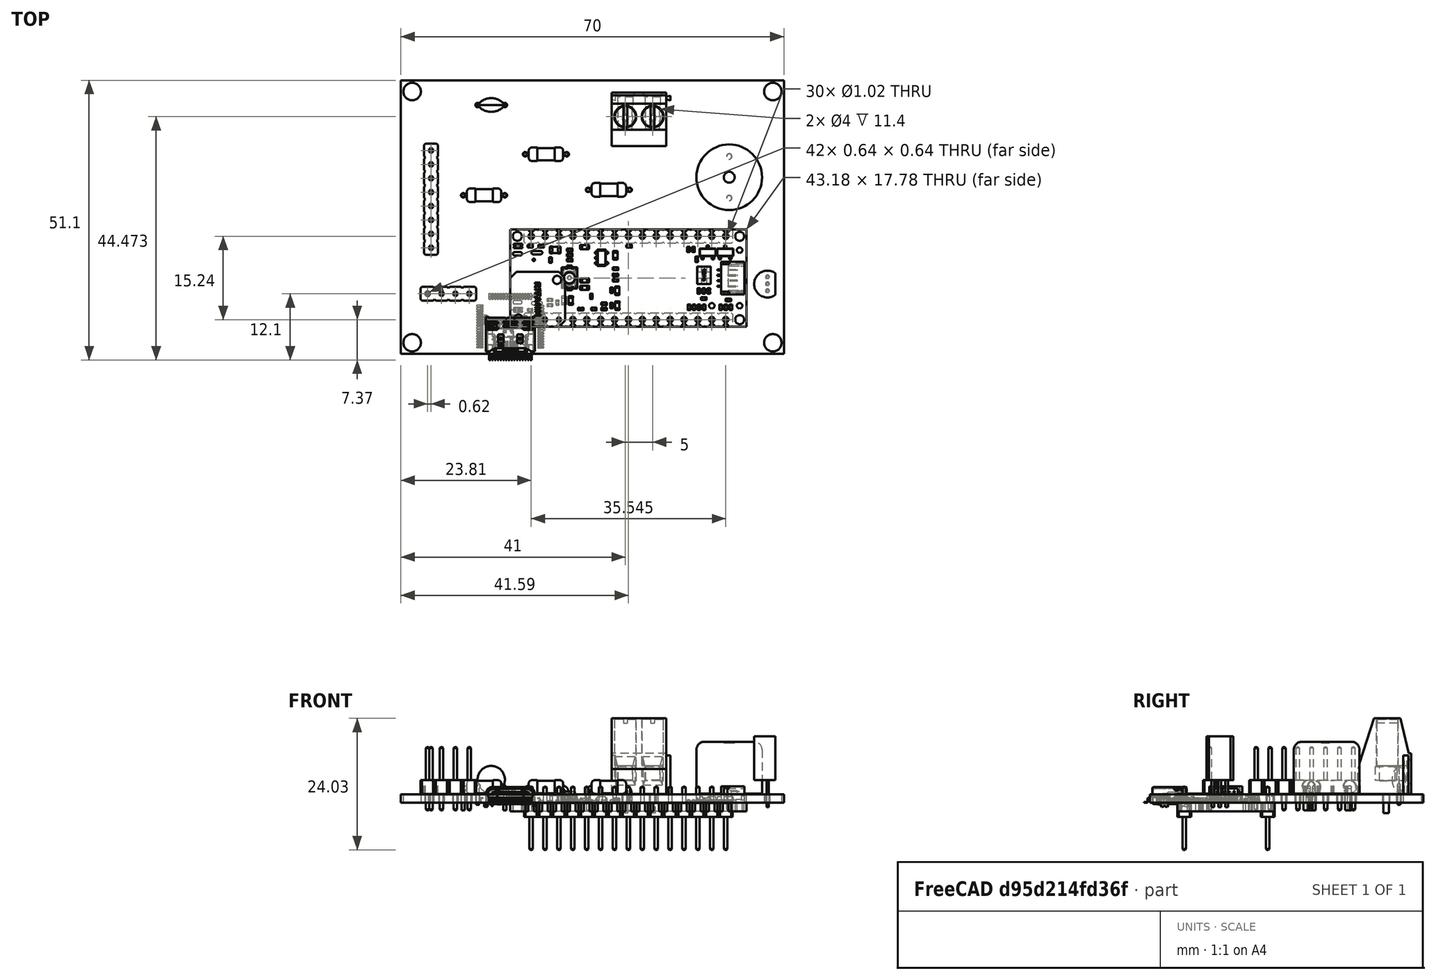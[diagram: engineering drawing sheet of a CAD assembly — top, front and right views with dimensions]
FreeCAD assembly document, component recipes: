
FREECAD ASSEMBLY — COMPONENT RECIPES ("assembly_Pendulum_fusion")

This assembly document has 14 components, labeled P0..P13 below (a component is one placed body or linked part). 12 of them carry a construction recipe — the FreeCAD feature program that regenerates the part from scratch, quoted from this document or its linked companion documents; the rest are supplied as boundary geometry only. No exploded tour is included for this assembly.
COMPONENT P0 — recipe-attached ("Body_Battery_Tattu", modeled in this document).
Construction recipe (the document's own serialized feature program — sketch geometry with constraints, then the solid features built on it; lengths are millimeters unless a unit is written):

FEATURE [Sketcher::SketchObject] Sketch048
  ArcFitTolerance = 1e-06
  AttachmentSupport = -> [XZ_Plane110]
  FullyConstrained = true
  MakeInternals = false
  MapMode = 5
  Placement = pos=(0,0,0) rot=(1,0,0;1.5708rad)
  sketch-geometry (6):
    g0: Circle CenterX=8.5 CenterY=-6.5 CenterZ=0 NormalX=0 NormalY=0 NormalZ=1 AngleXU=0 Radius=1.5
    g1: Circle CenterX=-8.5 CenterY=-6.5 CenterZ=0 NormalX=0 NormalY=0 NormalZ=1 AngleXU=0 Radius=1.5
    g2: Circle CenterX=-5.3 CenterY=-6.5 CenterZ=0 NormalX=0 NormalY=0 NormalZ=1 AngleXU=0 Radius=0.8
    g3: Circle CenterX=-2.8 CenterY=-6.5 CenterZ=0 NormalX=0 NormalY=0 NormalZ=1 AngleXU=0 Radius=0.8
    g4: Circle CenterX=2.8 CenterY=-6.5 CenterZ=0 NormalX=0 NormalY=0 NormalZ=1 AngleXU=0 Radius=0.8
    g5: Circle CenterX=5.3 CenterY=-6.5 CenterZ=0 NormalX=0 NormalY=0 NormalZ=1 AngleXU=0 Radius=0.8
  constraints (15):
    c: Equal(g0,g1)
    c: Equal(g5,g4)
    c: Equal(g4,g3)
    c: Equal(g3,g2)
    c: Symmetric(g0,g1,g-2)
    c: Diameter(g0) = 3
    c: DistanceX(g1,g0) = 17
    c: DistanceY(g0,g-1) = 6.5
    c: Diameter(g2) = 1.6
    c: Symmetric(g5,g2,g-2)
    c: Symmetric(g4,g3,g-2)
    c: DistanceX(g3,g4) = 5.6
    c: DistanceX(g2,g5) = 10.6
    c: DistanceY(g5,g-1) = 6.5
    c: DistanceY(g4,g-1) = 6.5
FEATURE [Sketcher::SketchObject] Sketch049
  ArcFitTolerance = 1e-06
  AttachmentSupport = -> [XZ_Plane110]
  FullyConstrained = true
  MakeInternals = false
  MapMode = 5
  Placement = pos=(0,0,0) rot=(1,0,0;1.5708rad)
  sketch-geometry (4):
    g0: LineSegment StartX=-10 StartY=8 StartZ=0 EndX=-10 EndY=-8 EndZ=0
    g1: LineSegment StartX=-10 StartY=-8 StartZ=0 EndX=10 EndY=-8 EndZ=0
    g2: LineSegment StartX=10 StartY=-8 StartZ=0 EndX=10 EndY=8 EndZ=0
    g3: LineSegment StartX=10 StartY=8 StartZ=0 EndX=-10 EndY=8 EndZ=0
  constraints (11):
    c: Coincident(g0,g1)
    c: Coincident(g1,g2)
    c: Coincident(g2,g3)
    c: Coincident(g3,g0)
    c: Vertical(g0)
    c: Vertical(g2)
    c: Horizontal(g1)
    c: Horizontal(g3)
    c: Symmetric(g1,g0,g-1)
    c: DistanceY(g0,g0) = 16
    c: DistanceX(g1,g1) = 20
FEATURE [PartDesign::Pad] Pad030
  Direction = (0,-1,2e-16)
  Length = 64.5
  Length2 = 10
  Placement = pos=(0,0,0) rot=(1,0,0;1.5708rad)
  Profile = -> Sketch049
  ReferenceAxis = -> Sketch049 [N_Axis]
  Refine = true
  Suppressed = false
  Type = 0
FEATURE [PartDesign::Fillet] Fillet007
  Base = -> Pad030 [Edge10,Edge4]
  BaseFeature = -> Pad030
  Placement = pos=(0,0,0) rot=(1,0,0;1.5708rad)
  Radius = 3
  Refine = true
  SupportTransform = false
  Suppressed = false
  UseAllEdges = false
FEATURE [PartDesign::Fillet] Fillet008
  Base = -> Fillet007 [Edge3,Edge13]
  BaseFeature = -> Fillet007
  Placement = pos=(0,0,0) rot=(1,0,0;1.5708rad)
  Radius = 9
  Refine = true
  SupportTransform = false
  Suppressed = false
  UseAllEdges = false
FEATURE [PartDesign::Pad] Pad031  label="Pad_Battery"
  BaseFeature = -> Fillet008
  Direction = (0,-1,2e-16)
  Length = 10
  Length2 = 10
  Midplane = true
  Placement = pos=(0,0,0) rot=(1,0,0;1.5708rad)
  Profile = -> Sketch048
  ReferenceAxis = -> Sketch048 [N_Axis]
  Refine = true
  Suppressed = false
  Type = 0
FEATURE [PartDesign::CoordinateSystem] Battery
  AttacherType = Attacher::AttachEngine3D
  AttachmentSupport = -> [Pad031]
  MapMode = 45
  Placement = pos=(-7,-64.5,2.89e-14) rot=(0,0,1;0rad)
FEATURE [PartDesign::Body] Body014  label="Body_Battery_Tattu"
  AllowCompound = false
  Group = -> [Sketch049,Pad030,Fillet007,Fillet008,Sketch048,Pad031,Battery]
  Origin = -> Origin110
  Tip = -> Pad031
COMPONENT P1 — recipe-attached ("Body_circuit_house", modeled in this document).
Construction recipe (the document's own serialized feature program — sketch geometry with constraints, then the solid features built on it; lengths are millimeters unless a unit is written):

FEATURE [Sketcher::SketchObject] Sketch064
  ArcFitTolerance = 1e-06
  AttachmentSupport = -> [XY_Plane115]
  FullyConstrained = false
  MakeInternals = false
  MapMode = 5
  sketch-geometry (4):
    g0: LineSegment StartX=-25.456 StartY=35.625 StartZ=0 EndX=-25.456 EndY=-34.975 EndZ=0
    g1: LineSegment StartX=-25.456 StartY=-34.975 StartZ=0 EndX=25.144 EndY=-34.975 EndZ=0
    g2: LineSegment StartX=25.144 StartY=-34.975 StartZ=0 EndX=25.144 EndY=35.625 EndZ=0
    g3: LineSegment StartX=25.144 StartY=35.625 StartZ=0 EndX=-25.456 EndY=35.625 EndZ=0
  constraints (10):
    c: Coincident(g0,g1)
    c: Coincident(g1,g2)
    c: Coincident(g2,g3)
    c: Coincident(g3,g0)
    c: Vertical(g0)
    c: Vertical(g2)
    c: Horizontal(g1)
    c: Horizontal(g3)
    c: DistanceX(g3,g3) = 50.6
    c: DistanceY(g0,g0) = 70.6
FEATURE [Sketcher::SketchObject] Sketch065
  ArcFitTolerance = 1e-06
  AttachmentSupport = -> [XY_Plane115]
  FullyConstrained = true
  MakeInternals = false
  MapMode = 5
  sketch-geometry (12):
    g0: LineSegment StartX=-22.96 StartY=27.96 StartZ=0 EndX=-22.96 EndY=-27.96 EndZ=0
    g1: LineSegment StartX=-17.96 StartY=-32.96 StartZ=0 EndX=17.96 EndY=-32.96 EndZ=0
    g2: LineSegment StartX=22.96 StartY=-27.96 StartZ=0 EndX=22.96 EndY=27.96 EndZ=0
    g3: LineSegment StartX=18.053 StartY=32 StartZ=0 EndX=-18.053 EndY=32 EndZ=0
    g4: LineSegment StartX=-27 StartY=37 StartZ=0 EndX=-27 EndY=-37 EndZ=0
    g5: LineSegment StartX=-27 StartY=-37 StartZ=0 EndX=27 EndY=-37 EndZ=0
    g6: LineSegment StartX=27 StartY=-37 StartZ=0 EndX=27 EndY=37 EndZ=0
    g7: LineSegment StartX=27 StartY=37 StartZ=0 EndX=-27 EndY=37 EndZ=0
    g8: ArcOfCircle CenterX=-22.96 CenterY=32.96 CenterZ=0 NormalX=0 NormalY=0 NormalZ=1 AngleXU=0 Radius=5 StartAngle=4.71239 EndAngle=6.08999
    g9: ArcOfCircle CenterX=22.96 CenterY=32.96 CenterZ=0 NormalX=0 NormalY=0 NormalZ=1 AngleXU=0 Radius=5 StartAngle=3.33479 EndAngle=4.71239
    g10: ArcOfCircle CenterX=22.96 CenterY=-32.96 CenterZ=0 NormalX=0 NormalY=0 NormalZ=1 AngleXU=0 Radius=5 StartAngle=1.5708 EndAngle=3.14159
    g11: ArcOfCircle CenterX=-22.96 CenterY=-32.96 CenterZ=0 NormalX=0 NormalY=0 NormalZ=1 AngleXU=0 Radius=5 StartAngle=3e-16 EndAngle=1.5708
  constraints (34):
    c: Coincident(g4,g5)
    c: Coincident(g5,g6)
    c: Coincident(g6,g7)
    c: Coincident(g7,g4)
    c: Vertical(g4)
    c: Vertical(g6)
    c: Horizontal(g5)
    c: Horizontal(g7)
    c: DistanceX(g7,g7) = 54
    c: DistanceY(g6,g6) = 74
    c: Symmetric(g4,g5,g-1)
    c: Equal(g8,g9)
    c: Equal(g9,g10)
    c: Equal(g10,g11)
    c: Diameter(g9) = 10
    c: Coincident(g3,g8)
    c: Coincident(g0,g8)
    c: Coincident(g3,g9)
    c: Coincident(g2,g9)
    c: Coincident(g0,g11)
    c: Coincident(g1,g11)
    c: Coincident(g1,g10)
    c: Coincident(g2,g10)
    c: Symmetric(g3,g3,g-2)
    c: Symmetric(g0,g0,g-1)
    c: Symmetric(g1,g1,g-2)
    c: Symmetric(g2,g2,g-1)
    c: Symmetric(g8,g10,g-1)
    c: DistanceY(g3,g4) = 5
    c: DistanceY(g10,g8) = 65.92
    c: DistanceX(g11,g10) = 45.92
    c: PointOnObject(g11,g1)
    c: PointOnObject(g8,g0)
    c: PointOnObject(g10,g2)
FEATURE [PartDesign::Pad] Pad040
  Direction = (0,0,1)
  Length = 26
  Length2 = 10
  Profile = -> Sketch065
  ReferenceAxis = -> Sketch065 [N_Axis]
  Refine = true
  Reversed = true
  Suppressed = false
  Type = 0
FEATURE [PartDesign::Pocket] Pocket019
  BaseFeature = -> Pad040
  Direction = (0,0,-1)
  Length = 2
  Length2 = 5
  Profile = -> Sketch064
  ReferenceAxis = -> Sketch064 [N_Axis]
  Refine = true
  Suppressed = false
  Type = 0
FEATURE [Sketcher::SketchObject] Sketch066
  ArcFitTolerance = 1e-06
  AttachmentSupport = -> [Pocket019]
  FullyConstrained = true
  MakeInternals = false
  MapMode = 5
  Placement = pos=(0,0,-2) rot=(0,0,1;0rad)
  sketch-geometry (4):
    g0: Circle CenterX=-22.96 CenterY=32.96 CenterZ=0 NormalX=0 NormalY=0 NormalZ=1 AngleXU=0 Radius=1.3
    g1: Circle CenterX=22.96 CenterY=32.96 CenterZ=0 NormalX=0 NormalY=0 NormalZ=1 AngleXU=0 Radius=1.3
    g2: Circle CenterX=22.96 CenterY=-32.96 CenterZ=0 NormalX=0 NormalY=0 NormalZ=1 AngleXU=0 Radius=1.3
    g3: Circle CenterX=-22.96 CenterY=-32.96 CenterZ=0 NormalX=0 NormalY=0 NormalZ=1 AngleXU=0 Radius=1.3
  constraints (9):
    c: Equal(g0,g1)
    c: Equal(g1,g2)
    c: Equal(g2,g3)
    c: Symmetric(g3,g0,g-1)
    c: Symmetric(g0,g1,g-2)
    c: Symmetric(g3,g2,g-2)
    c: DistanceX(g0,g1) = 45.92
    c: DistanceY(g2,g1) = 65.92
    c: Diameter(g0) = 2.6
FEATURE [PartDesign::Pocket] Pocket020
  BaseFeature = -> Pocket019
  Direction = (0,0,-1)
  Length = 5
  Length2 = 5
  Profile = -> Sketch066
  ReferenceAxis = -> Sketch066 [N_Axis]
  Refine = true
  Suppressed = false
  Type = 1
FEATURE [Sketcher::SketchObject] Sketch067
  ArcFitTolerance = 1e-06
  AttachmentSupport = -> [Pocket020]
  ExternalGeometry = -> [Pocket020]
  FullyConstrained = true
  MakeInternals = false
  MapMode = 5
  Placement = pos=(0,0,-26) rot=(1,0,0;3.14159rad)
  sketch-geometry (6):
    g0: ArcOfCircle CenterX=-27.5 CenterY=42 CenterZ=0 NormalX=0 NormalY=0 NormalZ=1 AngleXU=0 Radius=7 StartAngle=0 EndAngle=4.71239
    g1: ArcOfCircle CenterX=27.5 CenterY=42 CenterZ=0 NormalX=0 NormalY=0 NormalZ=1 AngleXU=0 Radius=7 StartAngle=4.71239 EndAngle=9.42478
    g2: LineSegment StartX=-20.5 StartY=42 StartZ=0 EndX=20.5 EndY=42 EndZ=0
    g3: LineSegment StartX=-27.5 StartY=35 StartZ=0 EndX=27.5 EndY=35 EndZ=0
    g4: Circle CenterX=-27.5 CenterY=42 CenterZ=0 NormalX=0 NormalY=0 NormalZ=1 AngleXU=0 Radius=2.3
    g5: Circle CenterX=27.5 CenterY=42 CenterZ=0 NormalX=0 NormalY=0 NormalZ=1 AngleXU=0 Radius=2.3
  constraints (16):
    c: Horizontal(g2)
    c: Symmetric(g0,g1,g-2)
    c: DistanceX(g0,g1) = 55
    c: Equal(g1,g0)
    c: Diameter(g1) = 14
    c: DistanceY(g-3,g0) = 5
    c: Horizontal(g3)
    c: PointOnObject(g0,g2)
    c: Coincident(g0,g3)
    c: Coincident(g0,g2)
    c: Coincident(g1,g2)
    c: Tangent(g1,g3) = -1.5708
    c: Coincident(g4,g0)
    c: Coincident(g5,g1)
    c: Equal(g5,g4)
    c: Diameter(g5) = 4.6
FEATURE [PartDesign::Pad] Pad041
  BaseFeature = -> Pocket020
  Direction = (0,0,-1)
  Length = 5
  Length2 = 10
  Profile = -> Sketch067
  ReferenceAxis = -> Sketch067 [N_Axis]
  Refine = true
  Reversed = true
  Suppressed = false
  Type = 0
FEATURE [PartDesign::CoordinateSystem] Circuit_House
  AttacherType = Attacher::AttachEngine3D
  AttachmentSupport = -> [Pad041]
  MapMode = 45
  Placement = pos=(27.5,-42,-21) rot=(0,0,0.999999;1.4e-05rad)
FEATURE [PartDesign::CoordinateSystem] Circuit_House_Top
  AttacherType = Attacher::AttachEngine3D
  AttachmentSupport = -> [Pad041]
  MapMode = 45
  Placement = pos=(-22.96,32.96,-2) rot=(0,0,1;0rad)
FEATURE [PartDesign::Body] Body018  label="Body_circuit_house"
  AllowCompound = false
  Group = -> [Sketch065,Pad040,Sketch064,Pocket019,Sketch066,Pocket020,Sketch067,Pad041,Circuit_House,Circuit_House_Top]
  Origin = -> Origin115
  Tip = -> Pad041
COMPONENT P2 — recipe-attached ("Body_Arm001", modeled in this document).
Construction recipe (the document's own serialized feature program — sketch geometry with constraints, then the solid features built on it; lengths are millimeters unless a unit is written):

FEATURE [Sketcher::SketchObject] Sketch006
  ArcFitTolerance = 1e-06
  AttachmentSupport = -> [XY_Plane004]
  FullyConstrained = true
  MakeInternals = false
  MapMode = 5
  sketch-geometry (1):
    g0: Circle CenterX=0 CenterY=84.85 CenterZ=0 NormalX=0 NormalY=0 NormalZ=1 AngleXU=0 Radius=23
  constraints (3):
    c: PointOnObject(g0,g-2)
    c: DistanceY(g-1,g0) = 84.85
    c: Diameter(g0) = 46
FEATURE [Sketcher::SketchObject] Sketch007
  ArcFitTolerance = 1e-06
  AttachmentSupport = -> [XY_Plane004]
  FullyConstrained = true
  MakeInternals = false
  MapMode = 5
  sketch-geometry (33):
    g0: LineSegment StartX=-18 StartY=67.5 StartZ=0 EndX=-18 EndY=-67.5 EndZ=0
    g1: LineSegment StartX=18 StartY=-67.5 StartZ=0 EndX=18 EndY=67.5 EndZ=0
    g2: ArcOfCircle CenterX=0 CenterY=84.8494 CenterZ=0 NormalX=0 NormalY=0 NormalZ=1 AngleXU=0 Radius=25 StartAngle=5.51619 EndAngle=10.1918
    g3: Circle CenterX=0 CenterY=84.8494 CenterZ=0 NormalX=0 NormalY=0 NormalZ=1 AngleXU=0 Radius=11.5
    g4: Circle CenterX=0 CenterY=99.8494 CenterZ=0 NormalX=0 NormalY=0 NormalZ=1 AngleXU=0 Radius=1.8
    g5: Circle CenterX=9.64181 CenterY=96.34 CenterZ=0 NormalX=0 NormalY=0 NormalZ=1 AngleXU=0 Radius=1.8
    g6: Circle CenterX=14.7721 CenterY=87.4541 CenterZ=0 NormalX=0 NormalY=0 NormalZ=1 AngleXU=0 Radius=1.8
    g7: Circle CenterX=12.9904 CenterY=77.3494 CenterZ=0 NormalX=0 NormalY=0 NormalZ=1 AngleXU=0 Radius=1.8
    g8: Circle CenterX=5.1303 CenterY=70.754 CenterZ=0 NormalX=0 NormalY=0 NormalZ=1 AngleXU=0 Radius=1.8
    g9: Circle CenterX=-5.1303 CenterY=70.754 CenterZ=0 NormalX=0 NormalY=0 NormalZ=1 AngleXU=0 Radius=1.8
    g10: Circle CenterX=-12.9904 CenterY=77.3494 CenterZ=0 NormalX=0 NormalY=0 NormalZ=1 AngleXU=0 Radius=1.8
    g11: Circle CenterX=-14.7721 CenterY=87.4541 CenterZ=0 NormalX=0 NormalY=0 NormalZ=1 AngleXU=0 Radius=1.8
    g12: Circle CenterX=-9.64181 CenterY=96.34 CenterZ=0 NormalX=0 NormalY=0 NormalZ=1 AngleXU=0 Radius=1.8
    g13: LineSegment [constr] StartX=-9.64181 StartY=96.34 StartZ=0 EndX=0 EndY=84.8494 EndZ=0
    g14: LineSegment [constr] StartX=-14.7721 StartY=87.4541 StartZ=0 EndX=0 EndY=84.8494 EndZ=0
    g15: LineSegment [constr] StartX=-12.9904 StartY=77.3494 StartZ=0 EndX=0 EndY=84.8494 EndZ=0
    g16: LineSegment [constr] StartX=-5.1303 StartY=70.754 StartZ=0 EndX=0 EndY=84.8494 EndZ=0
    g17: LineSegment [constr] StartX=5.1303 StartY=70.754 StartZ=0 EndX=0 EndY=84.8494 EndZ=0
    g18: LineSegment [constr] StartX=12.9904 StartY=77.3494 StartZ=0 EndX=0 EndY=84.8494 EndZ=0
    g19: LineSegment [constr] StartX=14.7721 StartY=87.4541 StartZ=0 EndX=0 EndY=84.8494 EndZ=0
    g20: LineSegment [constr] StartX=9.64181 StartY=96.34 StartZ=0 EndX=0 EndY=84.8494 EndZ=0
    g21: Circle CenterX=-7.78 CenterY=-27 CenterZ=0 NormalX=0 NormalY=0 NormalZ=1 AngleXU=0 Radius=1.8
    g22: Circle CenterX=7.78 CenterY=-27 CenterZ=0 NormalX=0 NormalY=0 NormalZ=1 AngleXU=0 Radius=1.8
    g23: ArcOfCircle CenterX=0 CenterY=-84.8494 CenterZ=0 NormalX=0 NormalY=0 NormalZ=1 AngleXU=0 Radius=25 StartAngle=2.3746 EndAngle=7.05018
    g24: Circle CenterX=0 CenterY=-84.8494 CenterZ=0 NormalX=0 NormalY=0 NormalZ=1 AngleXU=0 Radius=11.25
    g25: LineSegment StartX=-12.5 StartY=63.1987 StartZ=0 EndX=-12.5 EndY=-16.8013 EndZ=0
    g26: LineSegment StartX=-12.5 StartY=-16.8013 StartZ=0 EndX=12.5 EndY=-16.8013 EndZ=0
    g27: LineSegment StartX=12.5 StartY=-16.8013 StartZ=0 EndX=12.5 EndY=63.1987 EndZ=0
    g28: LineSegment StartX=-12.5 StartY=-33.5 StartZ=0 EndX=-12.5 EndY=-67.5 EndZ=0
    g29: LineSegment StartX=-12.5 StartY=-67.5 StartZ=0 EndX=12.5 EndY=-67.5 EndZ=0
    g30: LineSegment StartX=12.5 StartY=-67.5 StartZ=0 EndX=12.5 EndY=-33.5 EndZ=0
    g31: LineSegment StartX=12.5 StartY=-33.5 StartZ=0 EndX=-12.5 EndY=-33.5 EndZ=0
    g32: ArcOfCircle CenterX=0 CenterY=84.8494 CenterZ=0 NormalX=0 NormalY=0 NormalZ=1 AngleXU=0 Radius=25 StartAngle=4.18879 EndAngle=5.23599
  constraints (88):
    c: Vertical(g0)
    c: Vertical(g1)
    c: Symmetric(g0,g1,g-1)
    c: DistanceX(g0,g1) = 36
    c: DistanceY(g1,g1) = 135
    c: PointOnObject(g2,g-2)
    c: Diameter(g2) = 50
    c: Coincident(g2,g0)
    c: Coincident(g2,g1)
    c: Coincident(g3,g2)
    c: Diameter(g3) = 23
    c: PointOnObject(g4,g-2)
    c: Coincident(g13,g12)
    c: Coincident(g13,g2)
    c: Coincident(g14,g11)
    c: Coincident(g14,g2)
    c: Coincident(g15,g10)
    c: Coincident(g15,g2)
    c: Coincident(g16,g9)
    c: Coincident(g16,g2)
    c: Coincident(g17,g8)
    c: Coincident(g17,g2)
    c: Coincident(g18,g7)
    c: Coincident(g18,g2)
    c: Coincident(g19,g6)
    c: Coincident(g19,g2)
    c: Coincident(g20,g5)
    c: Coincident(g20,g2)
    c: Equal(g4,g5)
    c: Equal(g5,g6)
    c: Equal(g6,g7)
    c: Equal(g7,g8)
    c: Equal(g8,g9)
    c: Equal(g9,g10)
    c: Equal(g10,g11)
    c: Equal(g11,g12)
    c: Equal(g13,g14)
    c: Equal(g14,g15)
    c: Equal(g15,g16)
    c: Equal(g16,g17)
    c: Equal(g17,g18)
    c: Equal(g18,g19)
    c: Equal(g19,g20)
    c: DistanceY(g2,g4) = 15
    c: Distance(g13) = 15
    c: Diameter(g4) = 3.6
    c: Angle(g-2,g20) = 2.44346
    c: Angle(g19,g20) = 0.698132
    c: Angle(g18,g19) = 0.698132
    c: Angle(g17,g18) = 0.698132
    c: Angle(g16,g17) = 0.698132
    c: Angle(g15,g16) = 0.698132
    c: Angle(g14,g15) = 0.698132
    c: Angle(g13,g14) = 0.698132
    c: Equal(g22,g21)
    c: Diameter(g21) = 3.6
    c: DistanceX(g21,g22) = 15.56
    c: Symmetric(g21,g22,g-2)
    c: DistanceY(g22,g-1) = 27
    c: PointOnObject(g23,g-2)
    c: Diameter(g23) = 50
    c: Coincident(g23,g1)
    c: Coincident(g23,g0)
    c: Coincident(g24,g23)
    c: Diameter(g24) = 22.5
    c: Vertical(g25)
    c: Vertical(g27)
    c: Horizontal(g26)
    c: Coincident(g28,g29)
    c: Coincident(g29,g30)
    c: Coincident(g30,g31)
    c: Coincident(g31,g28)
    c: Vertical(g28)
    c: Vertical(g30)
    c: Horizontal(g29)
    c: Symmetric(g27,g25,g-2)
    c: DistanceY(g25,g25) = 80
    c: DistanceX(g25,g27) = 25
    c: PointOnObject(g1,g29)
    c: Symmetric(g28,g30,g-2)
    c: DistanceX(g31,g31) = 25
    c: DistanceY(g28,g28) = 34
    c: Diameter(g32) = 50
    c: Coincident(g32,g25)
    c: Coincident(g32,g27)
    c: Coincident(g32,g2)
    c: Coincident(g26,g25)
    c: Coincident(g27,g26)
FEATURE [PartDesign::Pad] Pad004  label="Pad_Arm"
  Direction = (0,0,1)
  Length = 8
  Length2 = 10
  Profile = -> Sketch007
  ReferenceAxis = -> Sketch007 [N_Axis]
  Refine = true
  Suppressed = false
  Type = 0
FEATURE [PartDesign::Pocket] Pocket001  label="Pocket_Motor"
  BaseFeature = -> Pad004
  Direction = (0,0,-1)
  Length = 3
  Length2 = 5
  Profile = -> Sketch006
  ReferenceAxis = -> Sketch006 [N_Axis]
  Refine = true
  Reversed = true
  Suppressed = false
  Type = 0
FEATURE [PartDesign::CoordinateSystem] Arm_Axis_Top
  AttacherType = Attacher::AttachEngine3D
  AttachmentOffset = pos=(0,0,0) rot=(0,0,-1;1.5708rad)
  AttachmentSupport = -> [Pocket001]
  MapMode = 11
  Placement = pos=(2e-16,99.8494,8) rot=(0,0,1;0rad)
FEATURE [PartDesign::CoordinateSystem] Arm_MPU6050_Right
  AttacherType = Attacher::AttachEngine3D
  AttachmentOffset = pos=(0,0,0) rot=(-1,0,0;1.5708rad)
  AttachmentSupport = -> [Pocket001]
  MapMode = 11
  Placement = pos=(-7.78,-27,0) rot=(-0.57735,-0.57735,0.57735;2.0944rad)
FEATURE [PartDesign::Chamfer] Chamfer002
  Angle = 45
  Base = -> Pocket001 [Edge42,Edge41]
  BaseFeature = -> Pocket001
  ChamferType = 0
  FlipDirection = false
  Refine = true
  Size = 1.5
  Size2 = 1
  SupportTransform = false
  Suppressed = false
  UseAllEdges = false
FEATURE [Sketcher::SketchObject] Sketch027
  ArcFitTolerance = 1e-06
  AttachmentSupport = -> [Chamfer002]
  ExternalGeometry = -> [Chamfer002]
  FullyConstrained = true
  MakeInternals = false
  MapMode = 5
  Placement = pos=(0,0,8) rot=(0,0,1;0rad)
  sketch-geometry (3):
    g0: ArcOfCircle CenterX=0 CenterY=-84.8494 CenterZ=0 NormalX=0 NormalY=0 NormalZ=1 AngleXU=0 Radius=25 StartAngle=2.3746 EndAngle=7.05018
    g1: LineSegment StartX=-18 StartY=-67.5 StartZ=0 EndX=18 EndY=-67.5 EndZ=0
    g2: Circle CenterX=0 CenterY=-84.8494 CenterZ=0 NormalX=0 NormalY=0 NormalZ=1 AngleXU=0 Radius=9
  constraints (7):
    c: Coincident(g0,g-3)
    c: Coincident(g1,g-3)
    c: Coincident(g0,g1)
    c: Coincident(g0,g1)
    c: Horizontal(g1)
    c: Coincident(g2,g0)
    c: Diameter(g2) = 18
FEATURE [PartDesign::Pad] Pad017  label="Pad_LockBearing"
  BaseFeature = -> Chamfer002
  Direction = (0,0,1)
  Length = 2
  Length2 = 10
  Profile = -> Sketch027
  ReferenceAxis = -> Sketch027 [N_Axis]
  Refine = true
  Reversed = true
  Suppressed = false
  Type = 0
FEATURE [Sketcher::SketchObject] Sketch032
  ArcFitTolerance = 1e-06
  AttachmentSupport = -> [Pad017]
  ExternalGeometry = -> [Pad017]
  FullyConstrained = true
  MakeInternals = false
  MapMode = 5
  Placement = pos=(0,0,8) rot=(0,0,1;0rad)
  sketch-geometry (3):
    g0: Circle CenterX=-15 CenterY=-75.5 CenterZ=0 NormalX=0 NormalY=0 NormalZ=1 AngleXU=0 Radius=1.8
    g1: Circle CenterX=15 CenterY=-75.5 CenterZ=0 NormalX=0 NormalY=0 NormalZ=1 AngleXU=0 Radius=1.8
    g2: Circle CenterX=0 CenterY=-105.5 CenterZ=0 NormalX=0 NormalY=0 NormalZ=1 AngleXU=0 Radius=1.8
  constraints (8):
    c: PointOnObject(g2,g-2)
    c: Equal(g2,g1)
    c: Equal(g1,g0)
    c: Diameter(g0) = 3.6
    c: DistanceY(g0,g-3) = 8
    c: DistanceY(g2,g0) = 30
    c: Symmetric(g0,g1,g-2)
    c: DistanceX(g0,g1) = 30
FEATURE [PartDesign::Pocket] Pocket009
  BaseFeature = -> Pad017
  Direction = (0,0,-1)
  Length = 5
  Length2 = 5
  Profile = -> Sketch032
  ReferenceAxis = -> Sketch032 [N_Axis]
  Refine = true
  Suppressed = false
  Type = 1
FEATURE [Sketcher::SketchObject] Sketch033
  ArcFitTolerance = 1e-06
  AttachmentSupport = -> [Pocket009]
  ExternalGeometry = -> [Pocket009]
  FullyConstrained = true
  MakeInternals = false
  MapMode = 5
  Placement = pos=(0,0,8) rot=(0,0,1;0rad)
  sketch-geometry (21):
    g0: LineSegment StartX=-13.35 StartY=-78.3579 StartZ=0 EndX=-11.7 EndY=-75.5 EndZ=0
    g1: LineSegment StartX=-11.7 StartY=-75.5 StartZ=0 EndX=-13.35 EndY=-72.6421 EndZ=0
    g2: LineSegment StartX=-13.35 StartY=-72.6421 StartZ=0 EndX=-16.65 EndY=-72.6421 EndZ=0
    g3: LineSegment StartX=-16.65 StartY=-72.6421 StartZ=0 EndX=-18.3 EndY=-75.5 EndZ=0
    g4: LineSegment StartX=-18.3 StartY=-75.5 StartZ=0 EndX=-16.65 EndY=-78.3579 EndZ=0
    g5: LineSegment StartX=-16.65 StartY=-78.3579 StartZ=0 EndX=-13.35 EndY=-78.3579 EndZ=0
    g6: Circle [constr] CenterX=-15 CenterY=-75.5 CenterZ=0 NormalX=0 NormalY=0 NormalZ=1 AngleXU=0 Radius=3.3
    g7: LineSegment StartX=16.65 StartY=-72.6421 StartZ=0 EndX=13.35 EndY=-72.6421 EndZ=0
    g8: LineSegment StartX=13.35 StartY=-72.6421 StartZ=0 EndX=11.7 EndY=-75.5 EndZ=0
    g9: LineSegment StartX=11.7 StartY=-75.5 StartZ=0 EndX=13.35 EndY=-78.3579 EndZ=0
    g10: LineSegment StartX=13.35 StartY=-78.3579 StartZ=0 EndX=16.65 EndY=-78.3579 EndZ=0
    g11: LineSegment StartX=16.65 StartY=-78.3579 StartZ=0 EndX=18.3 EndY=-75.5 EndZ=0
    g12: LineSegment StartX=18.3 StartY=-75.5 StartZ=0 EndX=16.65 EndY=-72.6421 EndZ=0
    g13: Circle [constr] CenterX=15 CenterY=-75.5 CenterZ=0 NormalX=0 NormalY=0 NormalZ=1 AngleXU=0 Radius=3.3
    g14: LineSegment StartX=1.65 StartY=-102.642 StartZ=0 EndX=-1.65 EndY=-102.642 EndZ=0
    g15: LineSegment StartX=-1.65 StartY=-102.642 StartZ=0 EndX=-3.3 EndY=-105.5 EndZ=0
    g16: LineSegment StartX=-3.3 StartY=-105.5 StartZ=0 EndX=-1.65 EndY=-108.358 EndZ=0
    g17: LineSegment StartX=-1.65 StartY=-108.358 StartZ=0 EndX=1.65 EndY=-108.358 EndZ=0
    g18: LineSegment StartX=1.65 StartY=-108.358 StartZ=0 EndX=3.3 EndY=-105.5 EndZ=0
    g19: LineSegment StartX=3.3 StartY=-105.5 StartZ=0 EndX=1.65 EndY=-102.642 EndZ=0
    g20: Circle [constr] CenterX=0 CenterY=-105.5 CenterZ=0 NormalX=0 NormalY=0 NormalZ=1 AngleXU=0 Radius=3.3
  constraints (48):
    c: Coincident(g0,g1)
    c: Coincident(g1,g2)
    c: Coincident(g2,g3)
    c: Coincident(g3,g4)
    c: Coincident(g4,g5)
    c: Coincident(g5,g0)
    c: Equal(g0, g1-g5) x5
    c: PointOnObject(g0,g6)
    c: PointOnObject(g1,g6)
    c: PointOnObject(g2,g6)
    c: PointOnObject(g3,g6)
    c: PointOnObject(g4,g6)
    c: PointOnObject(g5,g6)
    c: Coincident(g6,g-3)
    c: Coincident(g7,g8)
    c: Coincident(g8,g9)
    c: Coincident(g9,g10)
    c: Coincident(g10,g11)
    c: Coincident(g11,g12)
    c: Coincident(g12,g7)
    c: Equal(g7, g8-g12) x5
    c: PointOnObject(g7,g13)
    c: PointOnObject(g8,g13)
    c: PointOnObject(g9,g13)
    c: PointOnObject(g10,g13)
    c: PointOnObject(g11,g13)
    c: PointOnObject(g12,g13)
    c: Coincident(g13,g-4)
    c: Coincident(g14,g15)
    c: Coincident(g15,g16)
    c: Coincident(g16,g17)
    c: Coincident(g17,g18)
    c: Coincident(g18,g19)
    c: Coincident(g19,g14)
    c: Equal(g14, g15-g19) x5
    c: PointOnObject(g14,g20)
    c: PointOnObject(g15,g20)
    c: PointOnObject(g16,g20)
    c: PointOnObject(g17,g20)
    c: PointOnObject(g18,g20)
    c: PointOnObject(g19,g20)
    c: Coincident(g20,g-5)
    c: Equal(g13,g6)
    c: Equal(g6,g20)
    c: Diameter(g13) = 6.6
    c: Horizontal(g2)
    c: Horizontal(g7)
    c: Horizontal(g14)
FEATURE [PartDesign::Pocket] Pocket010
  BaseFeature = -> Pocket009
  Direction = (0,0,-1)
  Length = 3
  Length2 = 5
  Profile = -> Sketch033
  ReferenceAxis = -> Sketch033 [N_Axis]
  Refine = true
  Suppressed = false
  Type = 0
FEATURE [PartDesign::CoordinateSystem] Arm_Axis_Bottom
  AttacherType = Attacher::AttachEngine3D
  AttachmentSupport = -> [Pocket010]
  MapMode = 45
  Placement = pos=(4.26e-14,-84.8494,8) rot=(0,0,1;0rad)
FEATURE [PartDesign::Body] Body003  label="Body_Arm"
  AllowCompound = false
  Group = -> [Sketch007,Pad004,Sketch006,Pocket001,Arm_Axis_Top,Arm_MPU6050_Right,Chamfer002,Sketch027,Pad017,Sketch032,Pocket009,Sketch033,Pocket010,Arm_Axis_Bottom]
  Origin = -> Origin004
  Tip = -> Pocket010
COMPONENT P3 — recipe-attached ("Body_Bearing001", modeled in this document).
Construction recipe (the document's own serialized feature program — sketch geometry with constraints, then the solid features built on it; lengths are millimeters unless a unit is written):

FEATURE [Sketcher::SketchObject] Sketch005  label="Sketch_section"
  ArcFitTolerance = 0
  AttachmentSupport = -> [XZ_Plane003]
  FullyConstrained = true
  MakeInternals = false
  MapMode = 5
  Placement = pos=(0,0,0) rot=(1,0,0;1.5708rad)
  sketch-geometry (12):
    g0: LineSegment StartX=4 StartY=-3.5 StartZ=0 EndX=6.5 EndY=-3.5 EndZ=0
    g1: LineSegment StartX=11 StartY=-3.5 StartZ=0 EndX=11 EndY=3.5 EndZ=0
    g2: LineSegment StartX=11 StartY=3.5 StartZ=0 EndX=9.25 EndY=3.5 EndZ=0
    g3: LineSegment StartX=4 StartY=3.5 StartZ=0 EndX=4 EndY=-3.5 EndZ=0
    g4: LineSegment StartX=6.5 StartY=3.5 StartZ=0 EndX=6.75 EndY=3.25 EndZ=0
    g5: LineSegment StartX=6.75 StartY=3.25 StartZ=0 EndX=9 EndY=3.25 EndZ=0
    g6: LineSegment StartX=9 StartY=3.25 StartZ=0 EndX=9.25 EndY=3.5 EndZ=0
    g7: LineSegment StartX=6.5 StartY=-3.5 StartZ=0 EndX=6.75 EndY=-3.25 EndZ=0
    g8: LineSegment StartX=6.75 StartY=-3.25 StartZ=0 EndX=9 EndY=-3.25 EndZ=0
    g9: LineSegment StartX=9 StartY=-3.25 StartZ=0 EndX=9.25 EndY=-3.5 EndZ=0
    g10: LineSegment StartX=6.5 StartY=3.5 StartZ=0 EndX=4 EndY=3.5 EndZ=0
    g11: LineSegment StartX=9.25 StartY=-3.5 StartZ=0 EndX=11 EndY=-3.5 EndZ=0
  constraints (33):
    c: Coincident(g11,g1)
    c: Coincident(g1,g2)
    c: Coincident(g10,g3)
    c: Coincident(g3,g0)
    c: Horizontal(g0)
    c: Horizontal(g2)
    c: Vertical(g1)
    c: DistanceY(g1) = 7
    c: DistanceX(g0) = 4
    c: DistanceX(g11) = 11
    c: Coincident(g4,g5)
    c: Horizontal(g5)
    c: Coincident(g5,g6)
    c: Coincident(g7,g8)
    c: Horizontal(g8)
    c: Coincident(g8,g9)
    c: Coincident(g2,g6)
    c: Coincident(g10,g4)
    c: Tangent(g2,g10)
    c: Coincident(g0,g7)
    c: Coincident(g11,g9)
    c: Tangent(g0,g11)
    c: Equal(g4,g6)
    c: Equal(g6,g7)
    c: Angle(g10,g4) = 2.35619
    c: DistanceX(g2) = -1.75
    c: DistanceX(g10) = -2.5
    c: Equal(g0,g10)
    c: Equal(g11,g2)
    c: Equal(g9,g7)
    c: Parallel(g9,g4)
    c: DistanceY(g5,g1) = 0.25
    c: Symmetric(g0,g3,g-1)
FEATURE [PartDesign::Revolution] Revolution
  Angle = 360
  Angle2 = 60
  Axis = (0,2e-16,1)
  Base = (0,0,0)
  Placement = pos=(0,0,0) rot=(1,0,0;1.5708rad)
  Profile = -> Sketch005
  ReferenceAxis = -> Sketch005 [V_Axis]
  Refine = true
  Suppressed = false
  Type = 0
FEATURE [PartDesign::Chamfer] Chamfer
  Angle = 45
  Base = -> Revolution [Edge12,Edge11]
  BaseFeature = -> Revolution
  ChamferType = 0
  FlipDirection = false
  Placement = pos=(0,0,0) rot=(1,0,0;1.5708rad)
  Refine = true
  Size = 0.25
  Size2 = 1
  SupportTransform = false
  Suppressed = false
  UseAllEdges = false
FEATURE [PartDesign::CoordinateSystem] Bearing_Axis
  AttacherType = Attacher::AttachEngine3D
  AttachmentSupport = -> [Chamfer]
  MapMode = 45
  Placement = pos=(1.89e-14,1.7e-15,3.5) rot=(0,0,1;0rad)
FEATURE [PartDesign::Body] Body002  label="Body_Bearing"
  AllowCompound = false
  Group = -> [Sketch005,Revolution,Chamfer,Bearing_Axis]
  Origin = -> Origin003
  Tip = -> Chamfer
COMPONENT P4 — recipe-attached ("Body_BearingLock001", modeled in this document).
Construction recipe (the document's own serialized feature program — sketch geometry with constraints, then the solid features built on it; lengths are millimeters unless a unit is written):

FEATURE [Sketcher::SketchObject] Sketch030
  ArcFitTolerance = 1e-06
  AttachmentSupport = -> [XY_Plane009]
  FullyConstrained = true
  MakeInternals = false
  MapMode = 5
  sketch-geometry (6):
    g0: ArcOfCircle CenterX=0 CenterY=-84.8494 CenterZ=0 NormalX=0 NormalY=0 NormalZ=1 AngleXU=0 Radius=25 StartAngle=2.3746 EndAngle=7.05018
    g1: LineSegment StartX=18 StartY=-67.5 StartZ=0 EndX=-18 EndY=-67.5 EndZ=0
    g2: Circle CenterX=15.1 CenterY=-75.5 CenterZ=0 NormalX=0 NormalY=0 NormalZ=1 AngleXU=0 Radius=1.8
    g3: Circle CenterX=-15.1 CenterY=-75.5 CenterZ=0 NormalX=0 NormalY=0 NormalZ=1 AngleXU=0 Radius=1.8
    g4: Circle CenterX=0 CenterY=-105.5 CenterZ=0 NormalX=0 NormalY=0 NormalZ=1 AngleXU=0 Radius=1.8
    g5: Circle CenterX=0 CenterY=-84.8494 CenterZ=0 NormalX=0 NormalY=0 NormalZ=1 AngleXU=0 Radius=9
  constraints (17):
    c: PointOnObject(g0,g-2)
    c: Diameter(g0) = 50
    c: Horizontal(g1)
    c: Coincident(g0,g1)
    c: Coincident(g0,g1)
    c: DistanceX(g1,g1) = 36
    c: PointOnObject(g4,g-2)
    c: Equal(g3,g2)
    c: Equal(g2,g4)
    c: Diameter(g2) = 3.6
    c: Symmetric(g2,g3,g-2)
    c: DistanceX(g3,g2) = 30.2
    c: DistanceY(g2,g0) = 8
    c: DistanceY(g4,g2) = 30
    c: DistanceY(g0,g-1) = 67.5
    c: Coincident(g5,g0)
    c: Diameter(g5) = 18
FEATURE [PartDesign::Pad] Pad018
  Direction = (0,0,1)
  Length = 3
  Length2 = 10
  Profile = -> Sketch030
  ReferenceAxis = -> Sketch030 [N_Axis]
  Refine = true
  Reversed = true
  Suppressed = false
  Type = 0
FEATURE [PartDesign::CoordinateSystem] BearingLock
  AttacherType = Attacher::AttachEngine3D
  AttachmentOffset = pos=(0,0,0) rot=(0,0,-1;1.5708rad)
  AttachmentSupport = -> [Pad018]
  MapMode = 11
  Placement = pos=(0,-84.8494,-3) rot=(0,0,1;0rad)
FEATURE [Sketcher::SketchObject] Sketch031
  ArcFitTolerance = 1e-06
  AttachmentSupport = -> [Pad018]
  ExternalGeometry = -> [Pad018]
  FullyConstrained = true
  MakeInternals = false
  MapMode = 5
  Placement = pos=(0,0,-3) rot=(1,0,0;3.14159rad)
  sketch-geometry (2):
    g0: Circle CenterX=-15 CenterY=83.5 CenterZ=0 NormalX=0 NormalY=0 NormalZ=1 AngleXU=0 Radius=4
    g1: Circle CenterX=15 CenterY=83.5 CenterZ=0 NormalX=0 NormalY=0 NormalZ=1 AngleXU=0 Radius=4
  constraints (5):
    c: Equal(g0,g1)
    c: Diameter(g0) = 8
    c: Symmetric(g0,g1,g-2)
    c: DistanceX(g0,g1) = 30
    c: DistanceY(g-3,g0) = 8
FEATURE [PartDesign::Pad] Pad019
  BaseFeature = -> Pad018
  Direction = (0,0,-1)
  Length = 20
  Length2 = 10
  Profile = -> Sketch031
  ReferenceAxis = -> Sketch031 [N_Axis]
  Refine = true
  Suppressed = false
  Type = 0
FEATURE [PartDesign::Fillet] Fillet
  Base = -> Pad019 [Edge24,Edge22]
  BaseFeature = -> Pad019
  Radius = 3.5
  Refine = true
  SupportTransform = false
  Suppressed = false
  UseAllEdges = false
FEATURE [PartDesign::Body] Body007  label="Body_BearingLock"
  AllowCompound = false
  Group = -> [Sketch030,Pad018,BearingLock,Sketch031,Pad019,Fillet]
  Origin = -> Origin009
  Tip = -> Fillet
COMPONENT P5 — recipe-attached ("Body_MPU6051", modeled in this document).
Construction recipe (the document's own serialized feature program — sketch geometry with constraints, then the solid features built on it; lengths are millimeters unless a unit is written):

FEATURE [Sketcher::SketchObject] Sketch024
  ArcFitTolerance = 1e-06
  AttachmentSupport = -> [XZ_Plane008]
  FullyConstrained = true
  MakeInternals = false
  MapMode = 5
  Placement = pos=(0,0,0) rot=(1,0,0;1.5708rad)
  sketch-geometry (76):
    g0: LineSegment StartX=-8.94 StartY=-2.15 StartZ=0 EndX=-11.04 EndY=-2.15 EndZ=0
    g1: LineSegment StartX=-11.04 StartY=-2.15 StartZ=0 EndX=-11.04 EndY=-3.15 EndZ=0
    g2: LineSegment StartX=-11.04 StartY=-3.15 StartZ=0 EndX=-8.94 EndY=-3.15 EndZ=0
    g3: LineSegment StartX=-8.94 StartY=-3.15 StartZ=0 EndX=-8.94 EndY=-2.15 EndZ=0
    g4: LineSegment StartX=-8.94 StartY=-3.65 StartZ=0 EndX=-11.04 EndY=-3.65 EndZ=0
    g5: LineSegment StartX=-11.04 StartY=-3.65 StartZ=0 EndX=-11.04 EndY=-4.65 EndZ=0
    g6: LineSegment StartX=-11.04 StartY=-4.65 StartZ=0 EndX=-8.94 EndY=-4.65 EndZ=0
    g7: LineSegment StartX=-8.94 StartY=-4.65 StartZ=0 EndX=-8.94 EndY=-3.65 EndZ=0
    g8: LineSegment StartX=-8.94 StartY=-5.15 StartZ=0 EndX=-11.04 EndY=-5.15 EndZ=0
    g9: LineSegment StartX=-11.04 StartY=-5.15 StartZ=0 EndX=-11.04 EndY=-6.15 EndZ=0
    g10: LineSegment StartX=-11.04 StartY=-6.15 StartZ=0 EndX=-8.94 EndY=-6.15 EndZ=0
    g11: LineSegment StartX=-8.94 StartY=-6.15 StartZ=0 EndX=-8.94 EndY=-5.15 EndZ=0
    g12: LineSegment StartX=-5.34 StartY=-3.65 StartZ=0 EndX=-7.44 EndY=-3.65 EndZ=0
    g13: LineSegment StartX=-7.44 StartY=-3.65 StartZ=0 EndX=-7.44 EndY=-4.65 EndZ=0
    g14: LineSegment StartX=-7.44 StartY=-4.65 StartZ=0 EndX=-5.34 EndY=-4.65 EndZ=0
    g15: LineSegment StartX=-5.34 StartY=-4.65 StartZ=0 EndX=-5.34 EndY=-3.65 EndZ=0
    g16: LineSegment StartX=-5.34 StartY=-5.15 StartZ=0 EndX=-7.44 EndY=-5.15 EndZ=0
    g17: LineSegment StartX=-7.44 StartY=-5.15 StartZ=0 EndX=-7.44 EndY=-6.15 EndZ=0
    g18: LineSegment StartX=-7.44 StartY=-6.15 StartZ=0 EndX=-5.34 EndY=-6.15 EndZ=0
    g19: LineSegment StartX=-5.34 StartY=-6.15 StartZ=0 EndX=-5.34 EndY=-5.15 EndZ=0
    g20: LineSegment StartX=-1.68 StartY=-9.16 StartZ=0 EndX=-3.06 EndY=-9.16 EndZ=0
    g21: LineSegment StartX=-3.06 StartY=-9.16 StartZ=0 EndX=-3.06 EndY=-13.54 EndZ=0
    g22: LineSegment StartX=-3.06 StartY=-13.54 StartZ=0 EndX=-1.68 EndY=-13.54 EndZ=0
    g23: LineSegment StartX=-1.68 StartY=-13.54 StartZ=0 EndX=-1.68 EndY=-9.16 EndZ=0
    g24: LineSegment StartX=-4.18 StartY=-6.8 StartZ=0 EndX=-11.54 EndY=-6.8 EndZ=0
    g25: LineSegment StartX=-11.54 StartY=-6.8 StartZ=0 EndX=-11.54 EndY=-14.14 EndZ=0
    g26: LineSegment StartX=-11.54 StartY=-14.14 StartZ=0 EndX=-4.18 EndY=-14.14 EndZ=0
    g27: LineSegment StartX=-4.18 StartY=-14.14 StartZ=0 EndX=-4.18 EndY=-6.8 EndZ=0
    g28: LineSegment StartX=-4 StartY=-15.5 StartZ=0 EndX=-7.4 EndY=-15.5 EndZ=0
    g29: LineSegment StartX=-7.4 StartY=-15.5 StartZ=0 EndX=-7.4 EndY=-15.96 EndZ=0
    g30: LineSegment StartX=-7.4 StartY=-15.96 StartZ=0 EndX=-4 EndY=-15.96 EndZ=0
    g31: LineSegment StartX=-4 StartY=-15.96 StartZ=0 EndX=-4 EndY=-15.5 EndZ=0
    g32: LineSegment StartX=-8.9 StartY=-15.5 StartZ=0 EndX=-12.3 EndY=-15.5 EndZ=0
    g33: LineSegment StartX=-12.3 StartY=-15.5 StartZ=0 EndX=-12.3 EndY=-15.96 EndZ=0
    g34: LineSegment StartX=-12.3 StartY=-15.96 StartZ=0 EndX=-8.9 EndY=-15.96 EndZ=0
    g35: LineSegment StartX=-8.9 StartY=-15.96 StartZ=0 EndX=-8.9 EndY=-15.5 EndZ=0
    g36: LineSegment StartX=-8.9 StartY=-16.11 StartZ=0 EndX=-12.3 EndY=-16.11 EndZ=0
    g37: LineSegment StartX=-12.3 StartY=-16.11 StartZ=0 EndX=-12.3 EndY=-16.81 EndZ=0
    g38: LineSegment StartX=-12.3 StartY=-16.81 StartZ=0 EndX=-8.9 EndY=-16.81 EndZ=0
    g39: LineSegment StartX=-8.9 StartY=-16.81 StartZ=0 EndX=-8.9 EndY=-16.11 EndZ=0
    g40: LineSegment StartX=-4 StartY=-16.11 StartZ=0 EndX=-7.4 EndY=-16.11 EndZ=0
    g41: LineSegment StartX=-7.4 StartY=-16.11 StartZ=0 EndX=-7.4 EndY=-16.81 EndZ=0
    g42: LineSegment StartX=-7.4 StartY=-16.81 StartZ=0 EndX=-4 EndY=-16.81 EndZ=0
    g43: LineSegment StartX=-4 StartY=-16.81 StartZ=0 EndX=-4 EndY=-16.11 EndZ=0
    g44: LineSegment StartX=-4.78 StartY=-17.8 StartZ=0 EndX=-5.58 EndY=-17.8 EndZ=0
    g45: LineSegment StartX=-5.58 StartY=-17.8 StartZ=0 EndX=-5.58 EndY=-20.1 EndZ=0
    g46: LineSegment StartX=-5.58 StartY=-20.1 StartZ=0 EndX=-4.78 EndY=-20.1 EndZ=0
    g47: LineSegment StartX=-4.78 StartY=-20.1 StartZ=0 EndX=-4.78 EndY=-17.8 EndZ=0
    g48: LineSegment StartX=-10.88 StartY=-17.8 StartZ=0 EndX=-11.68 EndY=-17.8 EndZ=0
    g49: LineSegment StartX=-11.68 StartY=-17.8 StartZ=0 EndX=-11.68 EndY=-20.1 EndZ=0
    g50: LineSegment StartX=-11.68 StartY=-20.1 StartZ=0 EndX=-10.88 EndY=-20.1 EndZ=0
    g51: LineSegment StartX=-10.88 StartY=-20.1 StartZ=0 EndX=-10.88 EndY=-17.8 EndZ=0
    g52: LineSegment StartX=-6.28 StartY=-17.8 StartZ=0 EndX=-6.73 EndY=-17.8 EndZ=0
    g53: LineSegment StartX=-6.73 StartY=-18.12 StartZ=0 EndX=-6.28 EndY=-18.12 EndZ=0
    g54: LineSegment StartX=-6.28 StartY=-18.12 StartZ=0 EndX=-6.28 EndY=-17.8 EndZ=0
    g55: LineSegment StartX=-6.28 StartY=-19.72 StartZ=0 EndX=-6.73 EndY=-19.72 EndZ=0
    g56: LineSegment StartX=-6.73 StartY=-20.04 StartZ=0 EndX=-6.28 EndY=-20.04 EndZ=0
    g57: LineSegment StartX=-6.28 StartY=-20.04 StartZ=0 EndX=-6.28 EndY=-19.72 EndZ=0
    g58: LineSegment StartX=-9.17 StartY=-17.915 StartZ=0 EndX=-9.95 EndY=-17.915 EndZ=0
    g59: LineSegment StartX=-9.95 StartY=-17.915 StartZ=0 EndX=-9.95 EndY=-18.275 EndZ=0
    g60: LineSegment StartX=-9.95 StartY=-18.275 StartZ=0 EndX=-9.17 EndY=-18.275 EndZ=0
    g61: LineSegment StartX=-9.17 StartY=-18.74 StartZ=0 EndX=-9.95 EndY=-18.74 EndZ=0
    g62: LineSegment StartX=-9.95 StartY=-18.74 StartZ=0 EndX=-9.95 EndY=-19.1 EndZ=0
    g63: LineSegment StartX=-9.95 StartY=-19.1 StartZ=0 EndX=-9.17 EndY=-19.1 EndZ=0
    g64: LineSegment StartX=-9.17 StartY=-19.565 StartZ=0 EndX=-9.95 EndY=-19.565 EndZ=0
    g65: LineSegment StartX=-9.95 StartY=-19.565 StartZ=0 EndX=-9.95 EndY=-19.925 EndZ=0
    g66: LineSegment StartX=-9.95 StartY=-19.925 StartZ=0 EndX=-9.17 EndY=-19.925 EndZ=0
    g67: LineSegment StartX=-6.73 StartY=-17.45 StartZ=0 EndX=-9.17 EndY=-17.45 EndZ=0
    g68: LineSegment StartX=-9.17 StartY=-17.45 StartZ=0 EndX=-9.17 EndY=-17.915 EndZ=0
    g69: LineSegment StartX=-9.17 StartY=-20.39 StartZ=0 EndX=-6.73 EndY=-20.39 EndZ=0
    g70: LineSegment StartX=-6.73 StartY=-20.39 StartZ=0 EndX=-6.73 EndY=-20.04 EndZ=0
    g71: LineSegment StartX=-6.73 StartY=-17.8 StartZ=0 EndX=-6.73 EndY=-17.45 EndZ=0
    g72: LineSegment StartX=-6.73 StartY=-19.72 StartZ=0 EndX=-6.73 EndY=-18.12 EndZ=0
    g73: LineSegment StartX=-9.17 StartY=-18.275 StartZ=0 EndX=-9.17 EndY=-18.74 EndZ=0
    g74: LineSegment StartX=-9.17 StartY=-19.1 StartZ=0 EndX=-9.17 EndY=-19.565 EndZ=0
    g75: LineSegment StartX=-9.17 StartY=-19.925 StartZ=0 EndX=-9.17 EndY=-20.39 EndZ=0
  constraints (228):
    c: Coincident(g0,g1)
    c: Coincident(g1,g2)
    c: Coincident(g2,g3)
    c: Coincident(g3,g0)
    c: Horizontal(g0)
    c: Horizontal(g2)
    c: Vertical(g1)
    c: Vertical(g3)
    c: Coincident(g4,g5)
    c: Coincident(g5,g6)
    c: Coincident(g6,g7)
    c: Coincident(g7,g4)
    c: Horizontal(g4)
    c: Horizontal(g6)
    c: Vertical(g5)
    c: Vertical(g7)
    c: Coincident(g8,g9)
    c: Coincident(g9,g10)
    c: Coincident(g10,g11)
    c: Coincident(g11,g8)
    c: Horizontal(g8)
    c: Horizontal(g10)
    c: Vertical(g9)
    c: Vertical(g11)
    c: Coincident(g12,g13)
    c: Coincident(g13,g14)
    c: Coincident(g14,g15)
    c: Coincident(g15,g12)
    c: Horizontal(g12)
    c: Horizontal(g14)
    c: Vertical(g13)
    c: Vertical(g15)
    c: Coincident(g16,g17)
    c: Coincident(g17,g18)
    c: Coincident(g18,g19)
    c: Coincident(g19,g16)
    c: Horizontal(g16)
    c: Horizontal(g18)
    c: Vertical(g17)
    c: Vertical(g19)
    c: Coincident(g20,g21)
    c: Coincident(g21,g22)
    c: Coincident(g22,g23)
    c: Coincident(g23,g20)
    c: Horizontal(g20)
    c: Horizontal(g22)
    c: Vertical(g21)
    c: Vertical(g23)
    c: Coincident(g24,g25)
    c: Coincident(g25,g26)
    c: Coincident(g26,g27)
    c: Coincident(g27,g24)
    c: Horizontal(g24)
    c: Horizontal(g26)
    c: Vertical(g25)
    c: Vertical(g27)
    c: Coincident(g28,g29)
    c: Coincident(g29,g30)
    c: Coincident(g30,g31)
    c: Coincident(g31,g28)
    c: Horizontal(g28)
    c: Horizontal(g30)
    c: Vertical(g29)
    c: Vertical(g31)
    c: Coincident(g32,g33)
    c: Coincident(g33,g34)
    c: Coincident(g34,g35)
    c: Coincident(g35,g32)
    c: Horizontal(g32)
    c: Horizontal(g34)
    c: Vertical(g33)
    c: Vertical(g35)
    c: Coincident(g36,g37)
    c: Coincident(g37,g38)
    c: Coincident(g38,g39)
    c: Coincident(g39,g36)
    c: Horizontal(g36)
    c: Horizontal(g38)
    c: Vertical(g37)
    c: Vertical(g39)
    c: Coincident(g40,g41)
    c: Coincident(g41,g42)
    c: Coincident(g42,g43)
    c: Coincident(g43,g40)
    c: Horizontal(g40)
    c: Horizontal(g42)
    c: Vertical(g41)
    c: Vertical(g43)
    c: Coincident(g44,g45)
    c: Coincident(g45,g46)
    c: Coincident(g46,g47)
    c: Coincident(g47,g44)
    c: Horizontal(g44)
    c: Horizontal(g46)
    c: Vertical(g45)
    c: Vertical(g47)
    c: Coincident(g48,g49)
    c: Coincident(g49,g50)
    c: Coincident(g50,g51)
    c: Coincident(g51,g48)
    c: Horizontal(g48)
    c: Horizontal(g50)
    c: Vertical(g49)
    c: Vertical(g51)
    c: Coincident(g53,g54)
    c: Coincident(g54,g52)
    c: Horizontal(g52)
    c: Horizontal(g53)
    c: Vertical(g54)
    c: Coincident(g56,g57)
    c: Coincident(g57,g55)
    c: Horizontal(g55)
    c: Horizontal(g56)
    c: Vertical(g57)
    c: Coincident(g58,g59)
    c: Coincident(g59,g60)
    c: Horizontal(g58)
    c: Horizontal(g60)
    c: Vertical(g59)
    c: Coincident(g61,g62)
    c: Coincident(g62,g63)
    c: Horizontal(g61)
    c: Horizontal(g63)
    c: Vertical(g62)
    c: Coincident(g64,g65)
    c: Coincident(g65,g66)
    c: Horizontal(g64)
    c: Horizontal(g66)
    c: Vertical(g65)
    c: Coincident(g67,g68)
    c: Coincident(g75,g69)
    c: Coincident(g69,g70)
    c: Coincident(g71,g67)
    c: Horizontal(g67)
    c: Horizontal(g69)
    c: Vertical(g68)
    c: Vertical(g70)
    c: Equal(g0,g4)
    c: Equal(g4,g8)
    c: Equal(g8,g16)
    c: Equal(g16,g12)
    c: Equal(g19,g11)
    c: Equal(g11,g15)
    c: Equal(g15,g7)
    c: Equal(g7,g3)
    c: DistanceX(g0,g0) = 2.1
    c: DistanceY(g1,g1) = 1
    c: DistanceX(g0,g-1) = 8.94
    c: DistanceX(g4,g12) = 1.5
    c: DistanceY(g4,g1) = 0.5
    c: DistanceY(g8,g5) = 0.5
    c: PointOnObject(g17,g10)
    c: PointOnObject(g13,g6)
    c: PointOnObject(g13,g17)
    c: PointOnObject(g6,g11)
    c: DistanceY(g0,g-1) = 2.15
    c: PointOnObject(g4,g3)
    c: DistanceX(g24,g24) = 7.36
    c: DistanceY(g27,g27) = 7.34
    c: DistanceX(g24,g-1) = 4.18
    c: DistanceY(g24,g-1) = 6.8
    c: DistanceX(g20,g20) = 1.38
    c: DistanceY(g23,g23) = 4.38
    c: DistanceX(g20,g-1) = 1.68
    c: DistanceY(g20,g-1) = 9.16
    c: Equal(g28,g40)
    c: Equal(g40,g32)
    c: Equal(g32,g36)
    c: Equal(g29,g35)
    c: Equal(g43,g39)
    c: PointOnObject(g30,g43)
    c: PointOnObject(g34,g39)
    c: PointOnObject(g40,g36)
    c: PointOnObject(g29,g34)
    c: DistanceX(g28,g28) = 3.4
    c: DistanceY(g31,g31) = 0.46
    c: DistanceY(g40,g30) = 0.15
    c: DistanceY(g43,g43) = 0.7
    c: DistanceX(g32,g28) = 1.5
    c: DistanceX(g28,g-1) = 4
    c: DistanceY(g28,g-1) = 15.5
    c: Equal(g44,g48)
    c: Equal(g47,g51)
    c: PointOnObject(g44,g48)
    c: DistanceX(g46,g46) = 0.8
    c: DistanceY(g47,g47) = 2.3
    c: DistanceX(g46,g-1) = 4.78
    c: DistanceY(g44,g-1) = 17.8
    c: DistanceX(g50,g45) = 5.3
    c: Coincident(g72,g55)
    c: Coincident(g56,g70)
    c: Vertical(g72)
    c: PointOnObject(g56,g72)
    c: Vertical(g71)
    c: Coincident(g72,g53)
    c: Coincident(g52,g71)
    c: Coincident(g58,g68)
    c: Coincident(g73,g60)
    c: Coincident(g61,g73)
    c: Coincident(g74,g63)
    c: Coincident(g64,g74)
    c: Coincident(g66,g75)
    c: Vertical(g74)
    c: Vertical(g75)
    c: PointOnObject(g58,g73)
    c: Vertical(g73)
    c: PointOnObject(g61,g74)
    c: PointOnObject(g64,g75)
    c: Equal(g58,g61)
    c: Equal(g61,g64)
    c: Equal(g59,g62)
    c: Equal(g62,g65)
    c: Equal(g52,g55)
    c: Equal(g54,g57)
    c: Equal(g71,g70)
    c: Equal(g68,g73)
    c: Equal(g73,g74)
    c: Equal(g74,g75)
    c: DistanceY(g71,g71) = 0.35
    c: DistanceY(g54,g54) = 0.32
    c: PointOnObject(g52,g72)
    c: DistanceX(g52,g52) = 0.45
    c: DistanceX(g53,g44) = 0.7
    c: DistanceY(g72,g72) = 1.6
    c: PointOnObject(g52,g44)
    c: DistanceX(g67,g67) = 2.44
    c: DistanceX(g58,g58) = 0.78
    c: DistanceY(g59,g59) = 0.36
FEATURE [Sketcher::SketchObject] Sketch025
  ArcFitTolerance = 1e-06
  AttachmentSupport = -> [XZ_Plane008]
  FullyConstrained = true
  MakeInternals = false
  MapMode = 5
  Placement = pos=(0,0,0) rot=(1,0,0;1.5708rad)
  sketch-geometry (15):
    g0: LineSegment StartX=0 StartY=0 StartZ=0 EndX=-15.75 EndY=0 EndZ=0
    g1: LineSegment StartX=-15.75 StartY=0 StartZ=0 EndX=-15.75 EndY=-21.11 EndZ=0
    g2: LineSegment StartX=-15.75 StartY=-21.11 StartZ=0 EndX=0 EndY=-21.11 EndZ=0
    g3: LineSegment StartX=0 StartY=-21.11 StartZ=0 EndX=0 EndY=0 EndZ=0
    g4: Circle CenterX=-2.775 CenterY=-2.775 CenterZ=0 NormalX=0 NormalY=0 NormalZ=1 AngleXU=0 Radius=1.56
    g5: Circle CenterX=-2.775 CenterY=-18.335 CenterZ=0 NormalX=0 NormalY=0 NormalZ=1 AngleXU=0 Radius=1.56
    g6: Circle CenterX=-14.19 CenterY=-2.39 CenterZ=0 NormalX=0 NormalY=0 NormalZ=1 AngleXU=0 Radius=1.05
    g7: Circle CenterX=-14.19 CenterY=-4.73 CenterZ=0 NormalX=0 NormalY=0 NormalZ=1 AngleXU=0 Radius=1.05
    g8: Circle CenterX=-14.19 CenterY=-7.07 CenterZ=0 NormalX=0 NormalY=0 NormalZ=1 AngleXU=0 Radius=1.05
    g9: Circle CenterX=-14.19 CenterY=-9.41 CenterZ=0 NormalX=0 NormalY=0 NormalZ=1 AngleXU=0 Radius=1.05
    g10: Circle CenterX=-14.19 CenterY=-11.75 CenterZ=0 NormalX=0 NormalY=0 NormalZ=1 AngleXU=0 Radius=1.05
    g11: Circle CenterX=-14.19 CenterY=-14.09 CenterZ=0 NormalX=0 NormalY=0 NormalZ=1 AngleXU=0 Radius=1.05
    g12: Circle CenterX=-14.19 CenterY=-16.43 CenterZ=0 NormalX=0 NormalY=0 NormalZ=1 AngleXU=0 Radius=1.05
    g13: Circle CenterX=-14.19 CenterY=-18.77 CenterZ=0 NormalX=0 NormalY=0 NormalZ=1 AngleXU=0 Radius=1.05
    g14: LineSegment [constr] StartX=-14.19 StartY=0 StartZ=0 EndX=-14.19 EndY=-21.11 EndZ=0
  constraints (45):
    c: Coincident(g0,g1)
    c: Coincident(g1,g2)
    c: Coincident(g2,g3)
    c: Coincident(g3,g0)
    c: Horizontal(g0)
    c: Horizontal(g2)
    c: Vertical(g1)
    c: Vertical(g3)
    c: Coincident(g0,g-1)
    c: DistanceX(g2,g2) = 15.75
    c: DistanceY(g1,g1) = 21.11
    c: Equal(g5,g4)
    c: DistanceY(g5,g4) = 15.56
    c: Diameter(g4) = 3.12
    c: DistanceY(g4,g0) = 2.775
    c: DistanceX(g4,g0) = 2.775
    c: DistanceX(g5,g2) = 2.775
    c: Diameter(g6) = 2.1
    c: Equal(g6,g7)
    c: Equal(g7,g8)
    c: Equal(g8,g9)
    c: Equal(g9,g10)
    c: Equal(g10,g11)
    c: Equal(g11,g12)
    c: Equal(g12,g13)
    c: PointOnObject(g14,g0)
    c: PointOnObject(g14,g2)
    c: Vertical(g14)
    c: DistanceX(g0,g14) = 1.56
    c: PointOnObject(g6,g14)
    c: PointOnObject(g7,g14)
    c: PointOnObject(g8,g14)
    c: PointOnObject(g9,g14)
    c: PointOnObject(g10,g14)
    c: PointOnObject(g12,g14)
    c: PointOnObject(g11,g14)
    c: PointOnObject(g13,g14)
    c: DistanceY(g7,g6) = 2.34
    c: DistanceY(g8,g7) = 2.34
    c: DistanceY(g9,g8) = 2.34
    c: DistanceY(g10,g9) = 2.34
    c: DistanceY(g11,g10) = 2.34
    c: DistanceY(g12,g11) = 2.34
    c: DistanceY(g13,g12) = 2.34
    c: DistanceY(g6,g0) = 2.39
FEATURE [PartDesign::Pad] Pad014  label="Pad_Plate"
  Direction = (0,-1,2e-16)
  Length = 1
  Length2 = 10
  Placement = pos=(0,0,0) rot=(1,0,0;1.5708rad)
  Profile = -> Sketch025
  ReferenceAxis = -> Sketch025 [N_Axis]
  Refine = true
  Suppressed = false
  Type = 0
FEATURE [PartDesign::Pad] Pad015  label="Pad_Circuit1"
  BaseFeature = -> Pad014
  Direction = (0,-1,2e-16)
  Length = 0.5
  Length2 = 10
  Placement = pos=(0,0,0) rot=(1,0,0;1.5708rad)
  Profile = -> Sketch024
  ReferenceAxis = -> Sketch024 [N_Axis]
  Refine = true
  Reversed = true
  Suppressed = false
  Type = 0
FEATURE [Sketcher::SketchObject] Sketch026
  ArcFitTolerance = 1e-06
  AttachmentOffset = pos=(0,0,-0.5) rot=(0,0,1;0rad)
  AttachmentSupport = -> [XZ_Plane008]
  ExternalGeometry = -> [Pad015]
  FullyConstrained = true
  MakeInternals = false
  MapMode = 5
  Placement = pos=(0,0.5,-1e-16) rot=(1,0,0;1.5708rad)
  sketch-geometry (56):
    g0: LineSegment StartX=-9.44 StartY=-2.15 StartZ=0 EndX=-10.44 EndY=-2.15 EndZ=0
    g1: LineSegment StartX=-10.44 StartY=-2.15 StartZ=0 EndX=-10.44 EndY=-3.15 EndZ=0
    g2: LineSegment StartX=-10.44 StartY=-3.15 StartZ=0 EndX=-9.44 EndY=-3.15 EndZ=0
    g3: LineSegment StartX=-9.44 StartY=-3.15 StartZ=0 EndX=-9.44 EndY=-2.15 EndZ=0
    g4: LineSegment StartX=-5.84 StartY=-3.65 StartZ=0 EndX=-6.84 EndY=-3.65 EndZ=0
    g5: LineSegment StartX=-6.84 StartY=-3.65 StartZ=0 EndX=-6.84 EndY=-4.65 EndZ=0
    g6: LineSegment StartX=-6.84 StartY=-4.65 StartZ=0 EndX=-5.84 EndY=-4.65 EndZ=0
    g7: LineSegment StartX=-5.84 StartY=-4.65 StartZ=0 EndX=-5.84 EndY=-3.65 EndZ=0
    g8: LineSegment StartX=-9.44 StartY=-3.65 StartZ=0 EndX=-10.44 EndY=-3.65 EndZ=0
    g9: LineSegment StartX=-10.44 StartY=-3.65 StartZ=0 EndX=-10.44 EndY=-4.65 EndZ=0
    g10: LineSegment StartX=-10.44 StartY=-4.65 StartZ=0 EndX=-9.44 EndY=-4.65 EndZ=0
    g11: LineSegment StartX=-9.44 StartY=-4.65 StartZ=0 EndX=-9.44 EndY=-3.65 EndZ=0
    g12: LineSegment StartX=-9.44 StartY=-5.15 StartZ=0 EndX=-10.44 EndY=-5.15 EndZ=0
    g13: LineSegment StartX=-10.44 StartY=-5.15 StartZ=0 EndX=-10.44 EndY=-6.15 EndZ=0
    g14: LineSegment StartX=-10.44 StartY=-6.15 StartZ=0 EndX=-9.44 EndY=-6.15 EndZ=0
    g15: LineSegment StartX=-9.44 StartY=-6.15 StartZ=0 EndX=-9.44 EndY=-5.15 EndZ=0
    g16: LineSegment StartX=-5.84 StartY=-5.15 StartZ=0 EndX=-6.84 EndY=-5.15 EndZ=0
    g17: LineSegment StartX=-6.84 StartY=-5.15 StartZ=0 EndX=-6.84 EndY=-6.15 EndZ=0
    g18: LineSegment StartX=-6.84 StartY=-6.15 StartZ=0 EndX=-5.84 EndY=-6.15 EndZ=0
    g19: LineSegment StartX=-5.84 StartY=-6.15 StartZ=0 EndX=-5.84 EndY=-5.15 EndZ=0
    g20: LineSegment StartX=-1.68 StartY=-9.96 StartZ=0 EndX=-3.06 EndY=-9.96 EndZ=0
    g21: LineSegment StartX=-3.06 StartY=-9.96 StartZ=0 EndX=-3.06 EndY=-12.74 EndZ=0
    g22: LineSegment StartX=-3.06 StartY=-12.74 StartZ=0 EndX=-1.68 EndY=-12.74 EndZ=0
    g23: LineSegment StartX=-1.68 StartY=-12.74 StartZ=0 EndX=-1.68 EndY=-9.96 EndZ=0
    g24: LineSegment StartX=-4.82 StartY=-7.44 StartZ=0 EndX=-10.9 EndY=-7.44 EndZ=0
    g25: LineSegment StartX=-10.9 StartY=-7.44 StartZ=0 EndX=-10.9 EndY=-13.5 EndZ=0
    g26: LineSegment StartX=-10.9 StartY=-13.5 StartZ=0 EndX=-4.82 EndY=-13.5 EndZ=0
    g27: LineSegment StartX=-4.82 StartY=-13.5 StartZ=0 EndX=-4.82 EndY=-7.44 EndZ=0
    g28: LineSegment StartX=-4.8 StartY=-15.5 StartZ=0 EndX=-6.6 EndY=-15.5 EndZ=0
    g29: LineSegment StartX=-6.6 StartY=-15.5 StartZ=0 EndX=-6.6 EndY=-15.96 EndZ=0
    g30: LineSegment StartX=-6.6 StartY=-15.96 StartZ=0 EndX=-4.8 EndY=-15.96 EndZ=0
    g31: LineSegment StartX=-4.8 StartY=-15.96 StartZ=0 EndX=-4.8 EndY=-15.5 EndZ=0
    g32: LineSegment StartX=-4.8 StartY=-16.11 StartZ=0 EndX=-6.6 EndY=-16.11 EndZ=0
    g33: LineSegment StartX=-6.6 StartY=-16.11 StartZ=0 EndX=-6.6 EndY=-16.81 EndZ=0
    g34: LineSegment StartX=-6.6 StartY=-16.81 StartZ=0 EndX=-4.8 EndY=-16.81 EndZ=0
    g35: LineSegment StartX=-4.8 StartY=-16.81 StartZ=0 EndX=-4.8 EndY=-16.11 EndZ=0
    g36: LineSegment StartX=-9.5 StartY=-15.5 StartZ=0 EndX=-11.7 EndY=-15.5 EndZ=0
    g37: LineSegment StartX=-11.7 StartY=-15.5 StartZ=0 EndX=-11.7 EndY=-15.96 EndZ=0
    g38: LineSegment StartX=-11.7 StartY=-15.96 StartZ=0 EndX=-9.5 EndY=-15.96 EndZ=0
    g39: LineSegment StartX=-9.5 StartY=-15.96 StartZ=0 EndX=-9.5 EndY=-15.5 EndZ=0
    g40: LineSegment StartX=-9.5 StartY=-16.11 StartZ=0 EndX=-11.7 EndY=-16.11 EndZ=0
    g41: LineSegment StartX=-11.7 StartY=-16.11 StartZ=0 EndX=-11.7 EndY=-16.81 EndZ=0
    g42: LineSegment StartX=-11.7 StartY=-16.81 StartZ=0 EndX=-9.5 EndY=-16.81 EndZ=0
    g43: LineSegment StartX=-9.5 StartY=-16.81 StartZ=0 EndX=-9.5 EndY=-16.11 EndZ=0
    g44: LineSegment StartX=-4.78 StartY=-18.4 StartZ=0 EndX=-5.58 EndY=-18.4 EndZ=0
    g45: LineSegment StartX=-5.58 StartY=-18.4 StartZ=0 EndX=-5.58 EndY=-19.5 EndZ=0
    g46: LineSegment StartX=-5.58 StartY=-19.5 StartZ=0 EndX=-4.78 EndY=-19.5 EndZ=0
    g47: LineSegment StartX=-4.78 StartY=-19.5 StartZ=0 EndX=-4.78 EndY=-18.4 EndZ=0
    g48: LineSegment StartX=-6.98 StartY=-17.7 StartZ=0 EndX=-8.92 EndY=-17.7 EndZ=0
    g49: LineSegment StartX=-8.92 StartY=-17.7 StartZ=0 EndX=-8.92 EndY=-20.14 EndZ=0
    g50: LineSegment StartX=-8.92 StartY=-20.14 StartZ=0 EndX=-6.98 EndY=-20.14 EndZ=0
    g51: LineSegment StartX=-6.98 StartY=-20.14 StartZ=0 EndX=-6.98 EndY=-17.7 EndZ=0
    g52: LineSegment StartX=-10.88 StartY=-18.4 StartZ=0 EndX=-11.68 EndY=-18.4 EndZ=0
    g53: LineSegment StartX=-11.68 StartY=-18.4 StartZ=0 EndX=-11.68 EndY=-19.5 EndZ=0
    g54: LineSegment StartX=-11.68 StartY=-19.5 StartZ=0 EndX=-10.88 EndY=-19.5 EndZ=0
    g55: LineSegment StartX=-10.88 StartY=-19.5 StartZ=0 EndX=-10.88 EndY=-18.4 EndZ=0
  constraints (168):
    c: Coincident(g0,g1)
    c: Coincident(g1,g2)
    c: Coincident(g2,g3)
    c: Coincident(g3,g0)
    c: Horizontal(g0)
    c: Horizontal(g2)
    c: Vertical(g1)
    c: Vertical(g3)
    c: Coincident(g4,g5)
    c: Coincident(g5,g6)
    c: Coincident(g6,g7)
    c: Coincident(g7,g4)
    c: Horizontal(g4)
    c: Horizontal(g6)
    c: Vertical(g5)
    c: Vertical(g7)
    c: Coincident(g8,g9)
    c: Coincident(g9,g10)
    c: Coincident(g10,g11)
    c: Coincident(g11,g8)
    c: Horizontal(g8)
    c: Horizontal(g10)
    c: Vertical(g9)
    c: Vertical(g11)
    c: Coincident(g12,g13)
    c: Coincident(g13,g14)
    c: Coincident(g14,g15)
    c: Coincident(g15,g12)
    c: Horizontal(g12)
    c: Horizontal(g14)
    c: Vertical(g13)
    c: Vertical(g15)
    c: Coincident(g16,g17)
    c: Coincident(g17,g18)
    c: Coincident(g18,g19)
    c: Coincident(g19,g16)
    c: Horizontal(g16)
    c: Horizontal(g18)
    c: Vertical(g17)
    c: Vertical(g19)
    c: Coincident(g20,g21)
    c: Coincident(g21,g22)
    c: Coincident(g22,g23)
    c: Coincident(g23,g20)
    c: Horizontal(g20)
    c: Horizontal(g22)
    c: Vertical(g21)
    c: Vertical(g23)
    c: Coincident(g24,g25)
    c: Coincident(g25,g26)
    c: Coincident(g26,g27)
    c: Coincident(g27,g24)
    c: Horizontal(g24)
    c: Horizontal(g26)
    c: Vertical(g25)
    c: Vertical(g27)
    c: Coincident(g28,g29)
    c: Coincident(g29,g30)
    c: Coincident(g30,g31)
    c: Coincident(g31,g28)
    c: Horizontal(g28)
    c: Horizontal(g30)
    c: Vertical(g29)
    c: Vertical(g31)
    c: Coincident(g32,g33)
    c: Coincident(g33,g34)
    c: Coincident(g34,g35)
    c: Coincident(g35,g32)
    c: Horizontal(g32)
    c: Horizontal(g34)
    c: Vertical(g33)
    c: Vertical(g35)
    c: Coincident(g36,g37)
    c: Coincident(g37,g38)
    c: Coincident(g38,g39)
    c: Coincident(g39,g36)
    c: Horizontal(g36)
    c: Horizontal(g38)
    c: Vertical(g37)
    c: Vertical(g39)
    c: Coincident(g40,g41)
    c: Coincident(g41,g42)
    c: Coincident(g42,g43)
    c: Coincident(g43,g40)
    c: Horizontal(g40)
    c: Horizontal(g42)
    c: Vertical(g41)
    c: Vertical(g43)
    c: Coincident(g44,g45)
    c: Coincident(g45,g46)
    c: Coincident(g46,g47)
    c: Coincident(g47,g44)
    c: Horizontal(g44)
    c: Horizontal(g46)
    c: Vertical(g45)
    c: Vertical(g47)
    c: Coincident(g48,g49)
    c: Coincident(g49,g50)
    c: Coincident(g50,g51)
    c: Coincident(g51,g48)
    c: Horizontal(g48)
    c: Horizontal(g50)
    c: Vertical(g49)
    c: Vertical(g51)
    c: Coincident(g52,g53)
    c: Coincident(g53,g54)
    c: Coincident(g54,g55)
    c: Coincident(g55,g52)
    c: Horizontal(g52)
    c: Horizontal(g54)
    c: Vertical(g53)
    c: Vertical(g55)
    c: Equal(g0,g3)
    c: Equal(g3,g4)
    c: Equal(g4,g7)
    c: Equal(g7,g16)
    c: Equal(g16,g19)
    c: Equal(g19,g12)
    c: Equal(g12,g15)
    c: Equal(g15,g8)
    c: Equal(g8,g11)
    c: PointOnObject(g0,g-3)
    c: PointOnObject(g2,g-4)
    c: DistanceX(g-4,g1) = 0.6
    c: PointOnObject(g8,g-5)
    c: PointOnObject(g1,g9)
    c: PointOnObject(g12,g-6)
    c: PointOnObject(g9,g13)
    c: PointOnObject(g5,g17)
    c: PointOnObject(g4,g8)
    c: PointOnObject(g16,g12)
    c: DistanceX(g-7,g4) = 0.6
    c: DistanceX(g-8,g24) = 0.64
    c: DistanceY(g24,g-8) = 0.64
    c: DistanceX(g26,g-9) = 0.64
    c: DistanceY(g-9,g26) = 0.64
    c: PointOnObject(g20,g-11)
    c: PointOnObject(g20,g-10)
    c: DistanceY(g20,g-10) = 0.8
    c: DistanceY(g-10,g21) = 0.8
    c: DistanceX(g50,g-25) = 0.25
    c: DistanceY(g-25,g50) = 0.25
    c: DistanceY(g48,g-24) = 0.25
    c: DistanceX(g-24,g48) = 0.25
    c: PointOnObject(g28,g-12)
    c: PointOnObject(g29,g-13)
    c: DistanceX(g-12,g28) = 0.8
    c: DistanceX(g28,g-12) = 0.8
    c: PointOnObject(g32,g-14)
    c: PointOnObject(g33,g-15)
    c: PointOnObject(g29,g33)
    c: PointOnObject(g30,g35)
    c: PointOnObject(g36,g-16)
    c: PointOnObject(g37,g-17)
    c: DistanceX(g-16,g36) = 0.6
    c: DistanceX(g36,g-16) = 0.6
    c: PointOnObject(g40,g-18)
    c: PointOnObject(g41,g-19)
    c: PointOnObject(g37,g41)
    c: PointOnObject(g38,g43)
    c: PointOnObject(g52,g-23)
    c: PointOnObject(g54,g-22)
    c: DistanceY(g52,g-22) = 0.6
    c: DistanceY(g-23,g53) = 0.6
    c: PointOnObject(g44,g-20)
    c: PointOnObject(g46,g-21)
    c: PointOnObject(g44,g52)
    c: PointOnObject(g45,g54)
FEATURE [PartDesign::Pad] Pad016  label="Pad_Circuit2"
  BaseFeature = -> Pad015
  Direction = (0,-1,2e-16)
  Length = 1
  Length2 = 10
  Midplane = true
  Placement = pos=(0,0,0) rot=(1,0,0;1.5708rad)
  Profile = -> Sketch026
  ReferenceAxis = -> Sketch026 [N_Axis]
  Refine = true
  Suppressed = false
  Type = 0
FEATURE [PartDesign::CoordinateSystem] MPU6050
  AttacherType = Attacher::AttachEngine3D
  AttachmentOffset = pos=(0,0,0) rot=(-0.57735,0.57735,-0.57735;2.0944rad)
  AttachmentSupport = -> [Pad016]
  MapMode = 11
  Placement = pos=(-2.775,0,-2.775) rot=(0,0,1;0rad)
FEATURE [PartDesign::Body] Body006  label="Body_MPU6050"
  AllowCompound = false
  Group = -> [Sketch025,Pad014,Sketch024,Pad015,Sketch026,Pad016,MPU6050]
  Origin = -> Origin008
  Tip = -> Pad016
COMPONENT P6 — recipe-attached ("Body_Motor001", modeled in this document).
Construction recipe (the document's own serialized feature program — sketch geometry with constraints, then the solid features built on it; lengths are millimeters unless a unit is written):

FEATURE [Sketcher::SketchObject] Sketch016
  ArcFitTolerance = 1e-06
  AttachmentSupport = -> [XY_Plane006]
  FullyConstrained = true
  MakeInternals = false
  MapMode = 5
  sketch-geometry (8):
    g0: LineSegment StartX=-7.5 StartY=-8 StartZ=0 EndX=-7.5 EndY=-13 EndZ=0
    g1: LineSegment StartX=7.5 StartY=-13 StartZ=0 EndX=7.5 EndY=-8 EndZ=0
    g2: LineSegment StartX=7.5 StartY=-8 StartZ=0 EndX=-7.5 EndY=-8 EndZ=0
    g3: LineSegment StartX=-10 StartY=-13 StartZ=0 EndX=-10 EndY=-14.2 EndZ=0
    g4: LineSegment StartX=-10 StartY=-14.2 StartZ=0 EndX=10 EndY=-14.2 EndZ=0
    g5: LineSegment StartX=10 StartY=-14.2 StartZ=0 EndX=10 EndY=-13 EndZ=0
    g6: LineSegment StartX=10 StartY=-13 StartZ=0 EndX=7.5 EndY=-13 EndZ=0
    g7: LineSegment StartX=-7.5 StartY=-13 StartZ=0 EndX=-10 EndY=-13 EndZ=0
  constraints (21):
    c: Coincident(g1,g2)
    c: Coincident(g2,g0)
    c: Vertical(g0)
    c: Coincident(g3,g4)
    c: Coincident(g4,g5)
    c: Coincident(g5,g6)
    c: Coincident(g7,g3)
    c: Vertical(g3)
    c: Vertical(g5)
    c: Horizontal(g6)
    c: Coincident(g6,g1)
    c: Coincident(g0,g7)
    c: Symmetric(g0,g1,g-2)
    c: Symmetric(g3,g4,g-2)
    c: Symmetric(g0,g1,g-2)
    c: DistanceX(g2,g2) = 15
    c: DistanceX(g4,g4) = 20
    c: DistanceY(g3,g3) = 1.2
    c: Horizontal(g7)
    c: DistanceY(g0,g0) = 5
    c: DistanceY(g0,g-1) = 8
FEATURE [Sketcher::SketchObject] Sketch017
  ArcFitTolerance = 1e-06
  AttachmentOffset = pos=(0,0,42) rot=(0,0,1;0rad)
  AttachmentSupport = -> [XZ_Plane006]
  FullyConstrained = true
  MakeInternals = false
  MapMode = 5
  Placement = pos=(0,-42,9.3e-15) rot=(1,0,0;1.5708rad)
  sketch-geometry (5):
    g0: LineSegment StartX=-0.955065 StartY=5.41644 StartZ=0 EndX=0 EndY=0 EndZ=0
    g1: LineSegment StartX=0.955065 StartY=5.41644 StartZ=0 EndX=0 EndY=0 EndZ=0
    g2: LineSegment StartX=-0.955065 StartY=5.41644 StartZ=0 EndX=-0.2 EndY=4.76079 EndZ=0
    g3: LineSegment StartX=-0.2 StartY=4.76079 StartZ=0 EndX=0.2 EndY=4.76079 EndZ=0
    g4: LineSegment StartX=0.2 StartY=4.76079 StartZ=0 EndX=0.955065 EndY=5.41644 EndZ=0
  constraints (12):
    c: Coincident(g0,g-1)
    c: Coincident(g1,g0)
    c: Coincident(g3,g2)
    c: Coincident(g4,g3)
    c: Coincident(g4,g1)
    c: Symmetric(g3,g2,g-2)
    c: Coincident(g2,g0)
    c: Symmetric(g0,g1,g-2)
    c: Angle(g1,g0) = 0.349066
    c: DistanceX(g3,g3) = 0.4
    c: Distance(g1) = 5.5
    c: Distance(g4) = 1
FEATURE [Sketcher::SketchObject] Sketch018
  ArcFitTolerance = 1e-06
  AttachmentSupport = -> [XZ_Plane006]
  FullyConstrained = true
  MakeInternals = false
  MapMode = 5
  Placement = pos=(0,0,0) rot=(1,0,0;1.5708rad)
  sketch-geometry (1):
    g0: Circle CenterX=0 CenterY=0 CenterZ=0 NormalX=0 NormalY=0 NormalZ=1 AngleXU=0 Radius=21
  constraints (2):
    c: Coincident(g0,g-1)
    c: Diameter(g0) = 42
FEATURE [PartDesign::Pad] Pad008  label="Pad_Cylinder"
  Direction = (0,-1,2e-16)
  Length = 34
  Length2 = 10
  Placement = pos=(0,0,0) rot=(1,0,0;1.5708rad)
  Profile = -> Sketch018
  ReferenceAxis = -> Sketch018 [N_Axis]
  Refine = true
  Suppressed = false
  Type = 0
FEATURE [Sketcher::SketchObject] Sketch019
  ArcFitTolerance = 1e-06
  AttachmentSupport = -> [Pad008]
  FullyConstrained = true
  MakeInternals = false
  MapMode = 5
  Placement = pos=(0,-34,0) rot=(1,0,0;1.5708rad)
  sketch-geometry (1):
    g0: Circle CenterX=0 CenterY=0 CenterZ=0 NormalX=0 NormalY=0 NormalZ=1 AngleXU=0 Radius=7.5
  constraints (2):
    c: Coincident(g0,g-1)
    c: Diameter(g0) = 15
FEATURE [PartDesign::Pad] Pad009  label="Pad_Bearing"
  BaseFeature = -> Pad008
  Direction = (0,-1,2e-16)
  Length = 1.2
  Length2 = 10
  Placement = pos=(0,0,0) rot=(1,0,0;1.5708rad)
  Profile = -> Sketch019
  ReferenceAxis = -> Sketch019 [N_Axis]
  Refine = true
  Suppressed = false
  Type = 0
FEATURE [Sketcher::SketchObject] Sketch020
  ArcFitTolerance = 1e-06
  AttachmentSupport = -> [Pad009]
  FullyConstrained = true
  MakeInternals = false
  MapMode = 5
  Placement = pos=(0,-35.2,0) rot=(1,0,0;1.5708rad)
  sketch-geometry (1):
    g0: Circle CenterX=0 CenterY=0 CenterZ=0 NormalX=0 NormalY=0 NormalZ=1 AngleXU=0 Radius=3
  constraints (2):
    c: Coincident(g0,g-1)
    c: Diameter(g0) = 6
FEATURE [PartDesign::Pad] Pad010  label="Pad_Drive_Shaft"
  BaseFeature = -> Pad009
  Direction = (0,-1,2e-16)
  Length = 6.4
  Length2 = 10
  Placement = pos=(0,0,0) rot=(1,0,0;1.5708rad)
  Profile = -> Sketch020
  ReferenceAxis = -> Sketch020 [N_Axis]
  Refine = true
  Suppressed = false
  Type = 0
FEATURE [Sketcher::SketchObject] Sketch021
  ArcFitTolerance = 1e-06
  AttachmentSupport = -> [Pad010]
  FullyConstrained = true
  MakeInternals = false
  MapMode = 5
  Placement = pos=(0,-41.6,0) rot=(1,0,0;1.5708rad)
  sketch-geometry (1):
    g0: Circle CenterX=0 CenterY=0 CenterZ=0 NormalX=0 NormalY=0 NormalZ=1 AngleXU=0 Radius=7.5
  constraints (2):
    c: Coincident(g0,g-1)
    c: Diameter(g0) = 15
FEATURE [PartDesign::Pad] Pad011  label="Pad_Thrust001"
  BaseFeature = -> Pad010
  Direction = (0,-1,2e-16)
  Length = 1.3
  Length2 = 10
  Placement = pos=(0,0,0) rot=(1,0,0;1.5708rad)
  Profile = -> Sketch021
  ReferenceAxis = -> Sketch021 [N_Axis]
  Refine = true
  Suppressed = false
  Type = 0
FEATURE [PartDesign::Pad] Pad012  label="Pad_Tooth"
  BaseFeature = -> Pad011
  Direction = (0,-1,2e-16)
  Length = 12
  Length2 = 10
  Placement = pos=(0,0,0) rot=(1,0,0;1.5708rad)
  Profile = -> Sketch017
  ReferenceAxis = -> Sketch017 [N_Axis]
  Refine = true
  Suppressed = false
  Type = 0
FEATURE [PartDesign::PolarPattern] PolarPattern004  label="PolarPattern_Shaft"
  Angle = 360
  Axis = -> Sketch017 [N_Axis]
  BaseFeature = -> Pad012
  Mode = 0
  Occurrences = 18
  Offset = 120
  Originals = -> [Pad012]
  Placement = pos=(0,0,0) rot=(1,0,0;1.5708rad)
  Refine = true
  Suppressed = false
  TransformMode = 0
FEATURE [Sketcher::SketchObject] Sketch022
  ArcFitTolerance = 1e-06
  AttachmentSupport = -> [PolarPattern004]
  FullyConstrained = true
  MakeInternals = false
  MapMode = 5
  Placement = pos=(0,-34,0) rot=(1,0,0;1.5708rad)
  sketch-geometry (1):
    g0: Circle CenterX=0 CenterY=15 CenterZ=0 NormalX=0 NormalY=0 NormalZ=1 AngleXU=0 Radius=1.75
  constraints (3):
    c: PointOnObject(g0,g-2)
    c: Diameter(g0) = 3.5
    c: DistanceY(g-1,g0) = 15
FEATURE [PartDesign::Pocket] Pocket007  label="Pocket_Screw001"
  BaseFeature = -> PolarPattern004
  Direction = (0,1,-2e-16)
  Length = 5
  Length2 = 5
  Placement = pos=(0,0,0) rot=(1,0,0;1.5708rad)
  Profile = -> Sketch022
  ReferenceAxis = -> Sketch022 [N_Axis]
  Refine = true
  Suppressed = false
  Type = 0
FEATURE [PartDesign::PolarPattern] PolarPattern005  label="PolarPattern_Fixations"
  Angle = 360
  Axis = -> Sketch022 [N_Axis]
  BaseFeature = -> Pocket007
  Mode = 0
  Occurrences = 3
  Offset = 120
  Originals = -> [Pocket007]
  Placement = pos=(0,0,0) rot=(1,0,0;1.5708rad)
  Refine = true
  Suppressed = false
  TransformMode = 0
FEATURE [PartDesign::Pad] Pad013  label="Pad_Connector"
  BaseFeature = -> PolarPattern005
  Direction = (0,0,1)
  Length = 22
  Length2 = 10
  Placement = pos=(0,0,0) rot=(1,0,0;1.5708rad)
  Profile = -> Sketch016
  ReferenceAxis = -> Sketch016 [N_Axis]
  Refine = true
  Reversed = true
  Suppressed = false
  Type = 0
FEATURE [Sketcher::SketchObject] Sketch023
  ArcFitTolerance = 1e-06
  AttachmentSupport = -> [Pad013]
  ExternalGeometry = -> [Pad013]
  FullyConstrained = true
  MakeInternals = false
  MapMode = 5
  Placement = pos=(0,0,-22) rot=(1,0,0;3.14159rad)
  sketch-geometry (4):
    g0: LineSegment StartX=-6.5 StartY=12 StartZ=0 EndX=-6.5 EndY=9 EndZ=0
    g1: LineSegment StartX=-6.5 StartY=9 StartZ=0 EndX=6.5 EndY=9 EndZ=0
    g2: LineSegment StartX=6.5 StartY=9 StartZ=0 EndX=6.5 EndY=12 EndZ=0
    g3: LineSegment StartX=6.5 StartY=12 StartZ=0 EndX=-6.5 EndY=12 EndZ=0
  constraints (12):
    c: Coincident(g0,g1)
    c: Coincident(g1,g2)
    c: Coincident(g2,g3)
    c: Coincident(g3,g0)
    c: Vertical(g0)
    c: Vertical(g2)
    c: Horizontal(g1)
    c: Horizontal(g3)
    c: DistanceX(g-3,g0) = 1
    c: DistanceX(g1,g-4) = 1
    c: DistanceY(g-4,g1) = 1
    c: DistanceY(g0,g-3) = 1
FEATURE [PartDesign::Pocket] Pocket008  label="Pocket_Pins"
  BaseFeature = -> Pad013
  Direction = (0,0,1)
  Length = 5
  Length2 = 5
  Placement = pos=(0,0,0) rot=(1,0,0;1.5708rad)
  Profile = -> Sketch023
  ReferenceAxis = -> Sketch023 [N_Axis]
  Refine = true
  Suppressed = false
  Type = 0
FEATURE [PartDesign::Fillet] Fillet001  label="Fillet_Cylinder"
  Base = -> Pocket008 [Edge3,Edge1]
  BaseFeature = -> Pocket008
  Placement = pos=(0,0,0) rot=(1,0,0;1.5708rad)
  Radius = 3
  Refine = true
  SupportTransform = false
  Suppressed = false
  UseAllEdges = false
FEATURE [PartDesign::Fillet] Fillet002  label="Fillet_Thrust_Bearing"
  Base = -> Fillet001 [Edge61,Edge43]
  BaseFeature = -> Fillet001
  Placement = pos=(0,0,0) rot=(1,0,0;1.5708rad)
  Radius = 1
  Refine = true
  SupportTransform = false
  Suppressed = false
  UseAllEdges = false
FEATURE [PartDesign::CoordinateSystem] Motor
  AttacherType = Attacher::AttachEngine3D
  AttachmentOffset = pos=(0,0,0) rot=(-0.57735,0.57735,-0.57735;2.0944rad)
  AttachmentSupport = -> [Fillet002]
  MapMode = 11
  Placement = pos=(0,-34,15) rot=(0,0,1;0rad)
FEATURE [PartDesign::CoordinateSystem] Motor_Shaft001
  AttacherType = Attacher::AttachEngine3D
  AttachmentOffset = pos=(0,0,0) rot=(-0.57735,0.57735,-0.57735;2.0944rad)
  AttachmentSupport = -> [Fillet002]
  MapMode = 11
  Placement = pos=(0,-42.9,9.5e-15) rot=(0,0,1;0rad)
FEATURE [PartDesign::Body] Body005  label="Body_Motor"
  AllowCompound = false
  Group = -> [Sketch018,Pad008,Sketch019,Pad009,Sketch020,Pad010,Sketch021,Pad011,Sketch017,Pad012,PolarPattern004,Sketch022,Pocket007,PolarPattern005,Sketch016,Pad013,Sketch023,Pocket008,Fillet001,Fillet002,Motor,Motor_Shaft001]
  Origin = -> Origin006
  Tip = -> Fillet002
COMPONENT P7 — recipe-attached ("Body_Pedestral001", modeled in this document).
Construction recipe (the document's own serialized feature program — sketch geometry with constraints, then the solid features built on it; lengths are millimeters unless a unit is written):

FEATURE [Sketcher::SketchObject] Sketch054
  ArcFitTolerance = 1e-06
  AttachmentSupport = -> [XY_Plane112]
  FullyConstrained = true
  MakeInternals = false
  MapMode = 5
  sketch-geometry (1):
    g0: Circle CenterX=0 CenterY=0 CenterZ=0 NormalX=0 NormalY=0 NormalZ=1 AngleXU=0 Radius=30
  constraints (2):
    c: Diameter(g0) = 60
    c: Coincident(g-1,g0)
FEATURE [PartDesign::Pad] Pad034
  Direction = (0,0,1)
  Length = 30
  Length2 = 10
  Profile = -> Sketch054
  ReferenceAxis = -> Sketch054 [N_Axis]
  Refine = true
  Suppressed = false
  Type = 0
FEATURE [Sketcher::SketchObject] Sketch055
  ArcFitTolerance = 1e-06
  AttachmentSupport = -> [XZ_Plane112]
  ExternalGeometry = -> [Pad034]
  FullyConstrained = true
  MakeInternals = false
  MapMode = 5
  Placement = pos=(0,0,0) rot=(1,0,0;1.5708rad)
  sketch-geometry (8):
    g0: LineSegment StartX=62.9979 StartY=30 StartZ=0 EndX=197.788 EndY=-162.501 EndZ=0
    g1: LineSegment StartX=197.788 StartY=-162.501 StartZ=0 EndX=157.788 EndY=-162.501 EndZ=0
    g2: LineSegment StartX=157.788 StartY=-162.501 StartZ=0 EndX=30 EndY=20 EndZ=0
    g3: LineSegment StartX=-157.788 StartY=-162.501 StartZ=0 EndX=-197.788 EndY=-162.501 EndZ=0
    g4: LineSegment StartX=-197.788 StartY=-162.501 StartZ=0 EndX=-62.9979 EndY=30 EndZ=0
    g5: LineSegment StartX=-62.9979 StartY=30 StartZ=0 EndX=62.9979 EndY=30 EndZ=0
    g6: LineSegment StartX=30 StartY=20 StartZ=0 EndX=-30 EndY=20 EndZ=0
    g7: LineSegment StartX=-30 StartY=20 StartZ=0 EndX=-157.788 EndY=-162.501 EndZ=0
  constraints (21):
    c: Coincident(g0,g1)
    c: Horizontal(g1)
    c: Coincident(g1,g2)
    c: Parallel(g0,g2)
    c: DistanceX(g1,g1) = 40
    c: Distance(g0) = 235
    c: Angle(g-1,g2) = 2.18166
    c: PointOnObject(g2,g-3)
    c: Horizontal(g3)
    c: Coincident(g3,g4)
    c: Coincident(g4,g5)
    c: Coincident(g6,g7)
    c: Coincident(g7,g3)
    c: Symmetric(g3,g1,g-2)
    c: DistanceX(g3,g3) = 40
    c: Symmetric(g4,g0,g-2)
    c: Symmetric(g6,g2,g-2)
    c: Coincident(g5,g0)
    c: Coincident(g6,g2)
    c: DistanceY(g6,g4) = 10
    c: PointOnObject(g-3,g5)
FEATURE [PartDesign::Pad] Pad035
  BaseFeature = -> Pad034
  Direction = (0,-1,2e-16)
  Length = 50
  Length2 = 10
  Midplane = true
  Profile = -> Sketch055
  ReferenceAxis = -> Sketch055 [N_Axis]
  Refine = true
  Suppressed = false
  Type = 0
FEATURE [Sketcher::SketchObject] Sketch056
  ArcFitTolerance = 1e-06
  AttachmentSupport = -> [Pad035]
  FullyConstrained = true
  MakeInternals = false
  MapMode = 5
  Placement = pos=(0,0,30) rot=(0,0,1;0rad)
  sketch-geometry (1):
    g0: Circle CenterX=0 CenterY=0 CenterZ=0 NormalX=0 NormalY=0 NormalZ=1 AngleXU=0 Radius=25.3
  constraints (2):
    c: Coincident(g0,g-1)
    c: Diameter(g0) = 50.6
FEATURE [Sketcher::SketchObject] Sketch057
  ArcFitTolerance = 1e-06
  AttachmentOffset = pos=(0,0,0) rot=(0,1,0;2.0944rad)
  AttachmentSupport = -> [XZ_Plane112]
  FullyConstrained = true
  MakeInternals = false
  MapMode = 5
  Placement = pos=(0,0,0) rot=(0.377964,0.654654,0.654654;2.41886rad)
  sketch-geometry (6):
    g0: LineSegment StartX=0 StartY=30 StartZ=0 EndX=62.9979 EndY=30 EndZ=0
    g1: LineSegment StartX=62.9979 StartY=30 StartZ=0 EndX=197.788 EndY=-162.501 EndZ=0
    g2: LineSegment StartX=197.788 StartY=-162.501 StartZ=0 EndX=157.788 EndY=-162.501 EndZ=0
    g3: LineSegment StartX=157.788 StartY=-162.501 StartZ=0 EndX=30 EndY=20 EndZ=0
    g4: LineSegment StartX=30 StartY=20 StartZ=0 EndX=0 EndY=20 EndZ=0
    g5: LineSegment StartX=0 StartY=20 StartZ=0 EndX=0 EndY=30 EndZ=0
  constraints (18):
    c: PointOnObject(g0,g-2)
    c: Horizontal(g0)
    c: Coincident(g0,g1)
    c: Coincident(g1,g2)
    c: Horizontal(g2)
    c: Coincident(g2,g3)
    c: Coincident(g3,g4)
    c: Coincident(g4,g5)
    c: Coincident(g5,g0)
    c: Vertical(g5)
    c: Horizontal(g4)
    c: DistanceY(g5,g5) = 10
    c: DistanceX(g2,g2) = 40
    c: Angle(g-1,g3) = 2.18166
    c: Distance(g1) = 235
    c: Parallel(g3,g1)
    c: DistanceY(g-1,g4) = 20
    c: DistanceX(g4,g4) = 30
FEATURE [Sketcher::SketchObject] Sketch058
  ArcFitTolerance = 1e-06
  AttachmentOffset = pos=(0,0,0) rot=(0,1,0;1.0472rad)
  AttachmentSupport = -> [XZ_Plane112]
  FullyConstrained = true
  MakeInternals = false
  MapMode = 5
  Placement = pos=(0,0,0) rot=(0.774597,0.447214,0.447214;1.82348rad)
  sketch-geometry (6):
    g0: LineSegment StartX=0 StartY=30 StartZ=0 EndX=62.9979 EndY=30 EndZ=0
    g1: LineSegment StartX=62.9979 StartY=30 StartZ=0 EndX=197.788 EndY=-162.501 EndZ=0
    g2: LineSegment StartX=197.788 StartY=-162.501 StartZ=0 EndX=157.788 EndY=-162.501 EndZ=0
    g3: LineSegment StartX=157.788 StartY=-162.501 StartZ=0 EndX=30 EndY=20 EndZ=0
    g4: LineSegment StartX=30 StartY=20 StartZ=0 EndX=0 EndY=20 EndZ=0
    g5: LineSegment StartX=0 StartY=20 StartZ=0 EndX=0 EndY=30 EndZ=0
  constraints (18):
    c: PointOnObject(g0,g-2)
    c: Horizontal(g0)
    c: Coincident(g0,g1)
    c: Coincident(g1,g2)
    c: Horizontal(g2)
    c: Coincident(g2,g3)
    c: Coincident(g3,g4)
    c: Coincident(g4,g5)
    c: Coincident(g5,g0)
    c: Vertical(g5)
    c: Horizontal(g4)
    c: DistanceY(g5,g5) = 10
    c: DistanceX(g2,g2) = 40
    c: Angle(g-1,g3) = 2.18166
    c: Distance(g1) = 235
    c: Parallel(g3,g1)
    c: DistanceY(g-1,g4) = 20
    c: DistanceX(g4,g4) = 30
FEATURE [Sketcher::SketchObject] Sketch059
  ArcFitTolerance = 1e-06
  AttachmentOffset = pos=(0,0,-163) rot=(0,0,1;0rad)
  AttachmentSupport = -> [XY_Plane112]
  FullyConstrained = true
  MakeInternals = false
  MapMode = 5
  Placement = pos=(0,0,-163) rot=(0,0,1;0rad)
  sketch-geometry (6):
    g0: ArcOfCircle CenterX=0 CenterY=0 CenterZ=0 NormalX=0 NormalY=0 NormalZ=1 AngleXU=0 Radius=145 StartAngle=1.8326 EndAngle=3.40339
    g1: ArcOfCircle CenterX=0 CenterY=0 CenterZ=0 NormalX=0 NormalY=0 NormalZ=1 AngleXU=0 Radius=205 StartAngle=1.8326 EndAngle=3.40339
    g2: LineSegment [constr] StartX=0 StartY=0 StartZ=0 EndX=-212.504 EndY=-56.9402 EndZ=0
    g3: LineSegment [constr] StartX=0 StartY=0 StartZ=0 EndX=-56.9402 EndY=212.504 EndZ=0
    g4: ArcOfCircle CenterX=-169.037 CenterY=-45.2933 CenterZ=0 NormalX=0 NormalY=0 NormalZ=1 AngleXU=0 Radius=30 StartAngle=3.40339 EndAngle=6.54498
    g5: ArcOfCircle CenterX=-45.2933 CenterY=169.037 CenterZ=0 NormalX=0 NormalY=0 NormalZ=1 AngleXU=0 Radius=30 StartAngle=4.97419 EndAngle=8.11578
  constraints (20):
    c: Coincident(g0,g-1)
    c: Coincident(g2,g0)
    c: Coincident(g3,g1)
    c: Coincident(g1,g0)
    c: PointOnObject(g0,g2)
    c: PointOnObject(g1,g2)
    c: PointOnObject(g1,g3)
    c: Angle(g2,g-1) = 2.87979
    c: Angle(g-2,g3) = 0.261799
    c: Radius(g0) = 145
    c: Diameter(g5) = 60
    c: Coincident(g5,g1)
    c: Coincident(g5,g0)
    c: Diameter(g4) = 60
    c: Coincident(g4,g1)
    c: Coincident(g4,g0)
    c: PointOnObject(g4,g2)
    c: PointOnObject(g0,g3)
    c: Equal(g3,g2)
    c: Distance(g3) = 220
FEATURE [PartDesign::Pad] Pad036
  BaseFeature = -> Pad035
  Direction = (0,0,1)
  Length = 5
  Length2 = 10
  Profile = -> Sketch059
  ReferenceAxis = -> Sketch059 [N_Axis]
  Refine = true
  Suppressed = false
  Type = 0
FEATURE [Sketcher::SketchObject] Sketch004
  ArcFitTolerance = 1e-06
  AttachmentSupport = -> [Pad036]
  ExternalGeometry = -> [Pad036]
  FullyConstrained = true
  MakeInternals = false
  MapMode = 5
  Placement = pos=(0,0,-158) rot=(0,0,1;0rad)
  sketch-geometry (4):
    g0: ArcOfCircle CenterX=0 CenterY=0 CenterZ=0 NormalX=0 NormalY=0 NormalZ=1 AngleXU=0 Radius=145 StartAngle=6.02139 EndAngle=7.59218
    g1: ArcOfCircle CenterX=0 CenterY=0 CenterZ=0 NormalX=0 NormalY=0 NormalZ=1 AngleXU=0 Radius=205 StartAngle=6.02139 EndAngle=7.59218
    g2: ArcOfCircle CenterX=45.2933 CenterY=169.037 CenterZ=0 NormalX=0 NormalY=0 NormalZ=1 AngleXU=0 Radius=30 StartAngle=1.309 EndAngle=4.45059
    g3: ArcOfCircle CenterX=169.037 CenterY=-45.2933 CenterZ=0 NormalX=0 NormalY=0 NormalZ=1 AngleXU=0 Radius=30 StartAngle=2.87979 EndAngle=6.02139
  constraints (11):
    c: Coincident(g0,g-1)
    c: Coincident(g1,g0)
    c: Symmetric(g-3,g0,g-2)
    c: Symmetric(g1,g-3,g-2)
    c: Coincident(g2,g1)
    c: Coincident(g2,g0)
    c: Coincident(g3,g1)
    c: Coincident(g3,g0)
    c: Radius(g2) = 30
    c: Radius(g3) = 30
    c: Symmetric(g-4,g3,g-2)
FEATURE [PartDesign::Pad] Pad003
  BaseFeature = -> Pad036
  Direction = (0,0,1)
  Length = 5
  Length2 = 10
  Profile = -> Sketch004
  ReferenceAxis = -> Sketch004 [N_Axis]
  Refine = true
  Reversed = true
  Suppressed = false
  Type = 0
FEATURE [PartDesign::Pad] Pad037
  BaseFeature = -> Pad003
  Direction = (0.866025,-0.5,1e-16)
  Length = 50
  Length2 = 10
  Midplane = true
  Profile = -> Sketch058
  ReferenceAxis = -> Sketch058 [N_Axis]
  Refine = true
  Suppressed = false
  Type = 0
FEATURE [PartDesign::Pad] Pad038
  BaseFeature = -> Pad037
  Direction = (0.866025,0.5,-1e-16)
  Length = 50
  Length2 = 10
  Midplane = true
  Profile = -> Sketch057
  ReferenceAxis = -> Sketch057 [N_Axis]
  Refine = true
  Suppressed = false
  Type = 0
FEATURE [PartDesign::Pocket] Pocket017
  BaseFeature = -> Pad038
  Direction = (0,0,-1)
  Length = 5
  Length2 = 5
  Profile = -> Sketch056
  ReferenceAxis = -> Sketch056 [N_Axis]
  Refine = true
  Suppressed = false
  Type = 1
FEATURE [Sketcher::SketchObject] Sketch060
  ArcFitTolerance = 1e-06
  AttachmentSupport = -> [Pad003]
  FullyConstrained = true
  MakeInternals = false
  MapMode = 5
  Placement = pos=(0,0,-158) rot=(0,0,1;0rad)
  sketch-geometry (5):
    g0: LineSegment StartX=-120.651 StartY=158.973 StartZ=0 EndX=-77.3494 EndY=183.973 EndZ=0
    g1: LineSegment StartX=-77.3494 StartY=183.973 StartZ=0 EndX=-57.3494 EndY=149.332 EndZ=0
    g2: LineSegment StartX=-57.3494 StartY=149.332 StartZ=0 EndX=-100.651 EndY=124.332 EndZ=0
    g3: LineSegment StartX=-100.651 StartY=124.332 StartZ=0 EndX=-120.651 EndY=158.973 EndZ=0
    g4: LineSegment [constr] StartX=0 StartY=0 StartZ=0 EndX=-115 EndY=199.186 EndZ=0
  constraints (13):
    c: Coincident(g0,g1)
    c: Coincident(g1,g2)
    c: Coincident(g2,g3)
    c: Coincident(g3,g0)
    c: Coincident(g4,g-1)
    c: Angle(g-1,g4) = 2.0944
    c: Symmetric(g0,g0,g4)
    c: Distance(g0) = 50
    c: Parallel(g1,g3)
    c: Distance(g3) = 40
    c: Distance(g4,g2) = 158
    c: Symmetric(g1,g2,g4)
    c: Distance(g4) = 230
FEATURE [PartDesign::CoordinateSystem] Pedestral_Top
  AttacherType = Attacher::AttachEngine3D
  AttachmentOffset = pos=(0,0,0) rot=(0,0,1;-0.523599rad)
  AttachmentSupport = -> [Pocket017]
  MapMode = 45
  Placement = pos=(1.208e-13,1.4e-15,30) rot=(0,0,1;5.75959rad)
FEATURE [PartDesign::Body] Body016  label="Body_Pedestral"
  AllowCompound = false
  Group = -> [Sketch054,Pad034,Sketch055,Pad035,Sketch056,Sketch059,Pad036,Sketch004,Pad003,Sketch060,Sketch058,Pad037,Sketch057,Pad038,Pocket017,Pedestral_Top]
  Origin = -> Origin112
  Tip = -> Pocket017
COMPONENT P8 — recipe-attached ("Body_Pedestral_Connector001", modeled in this document).
Construction recipe (the document's own serialized feature program — sketch geometry with constraints, then the solid features built on it; lengths are millimeters unless a unit is written):

FEATURE [Sketcher::SketchObject] Sketch061
  ArcFitTolerance = 1e-06
  AttachmentSupport = -> [YZ_Plane113]
  FullyConstrained = true
  MakeInternals = false
  MapMode = 5
  Placement = pos=(0,0,0) rot=(0.57735,0.57735,0.57735;2.0944rad)
  sketch-geometry (1):
    g0: Circle CenterX=0 CenterY=41 CenterZ=0 NormalX=0 NormalY=0 NormalZ=1 AngleXU=0 Radius=2.3
  constraints (3):
    c: PointOnObject(g0,g-2)
    c: Diameter(g0) = 4.6
    c: DistanceY(g-1,g0) = 41
FEATURE [Sketcher::SketchObject] Sketch062
  ArcFitTolerance = 1e-06
  AttachmentSupport = -> [XY_Plane113]
  FullyConstrained = true
  MakeInternals = false
  MapMode = 5
  sketch-geometry (2):
    g0: Circle CenterX=0 CenterY=0 CenterZ=0 NormalX=0 NormalY=0 NormalZ=1 AngleXU=0 Radius=25
    g1: Circle CenterX=0 CenterY=0 CenterZ=0 NormalX=0 NormalY=0 NormalZ=1 AngleXU=0 Radius=23
  constraints (4):
    c: Coincident(g0,g-1)
    c: Coincident(g1,g0)
    c: Diameter(g1) = 46
    c: Diameter(g0) = 50
FEATURE [PartDesign::Pad] Pad039
  Direction = (0,0,1)
  Length = 70
  Length2 = 10
  Profile = -> Sketch062
  ReferenceAxis = -> Sketch062 [N_Axis]
  Refine = true
  Suppressed = false
  Type = 0
FEATURE [PartDesign::Pocket] Pocket018
  BaseFeature = -> Pad039
  Direction = (-1,0,0)
  Length = 5
  Length2 = 5
  Profile = -> Sketch061
  ReferenceAxis = -> Sketch061 [N_Axis]
  Refine = true
  Suppressed = false
  Type = 1
FEATURE [PartDesign::CoordinateSystem] Pedestral_Connector
  AttacherType = Attacher::AttachEngine3D
  AttachmentOffset = pos=(0,0,0) rot=(0,0,-1;1.5708rad)
  AttachmentSupport = -> [Pocket018]
  MapMode = 11
  Placement = pos=(0,0,70) rot=(0,0,1;0rad)
FEATURE [PartDesign::Body] Body017  label="Body_Pedestral_Connector"
  AllowCompound = false
  Group = -> [Sketch061,Sketch062,Pad039,Pocket018,Pedestral_Connector]
  Origin = -> Origin113
  Tip = -> Pocket018
COMPONENT P9 — recipe-attached ("Body_ReactionWheel001", modeled in this document).
Construction recipe (the document's own serialized feature program — sketch geometry with constraints, then the solid features built on it; lengths are millimeters unless a unit is written):

FEATURE [Sketcher::SketchObject] Sketch008
  ArcFitTolerance = 1e-06
  AttachmentSupport = -> [XZ_Plane005]
  FullyConstrained = true
  MakeInternals = false
  MapMode = 5
  Placement = pos=(0,0,0) rot=(1,0,0;1.5708rad)
  sketch-geometry (8):
    g0: LineSegment StartX=-3.7 StartY=11.6 StartZ=0 EndX=-3.7 EndY=8 EndZ=0
    g1: LineSegment StartX=-3.7 StartY=8 StartZ=0 EndX=3.7 EndY=8 EndZ=0
    g2: LineSegment StartX=3.7 StartY=8 StartZ=0 EndX=3.7 EndY=11.6 EndZ=0
    g3: LineSegment StartX=3.7 StartY=11.6 StartZ=0 EndX=-3.7 EndY=11.6 EndZ=0
    g4: LineSegment StartX=-3.7 StartY=-8 StartZ=0 EndX=-3.7 EndY=-11.6 EndZ=0
    g5: LineSegment StartX=-3.7 StartY=-11.6 StartZ=0 EndX=3.7 EndY=-11.6 EndZ=0
    g6: LineSegment StartX=3.7 StartY=-11.6 StartZ=0 EndX=3.7 EndY=-8 EndZ=0
    g7: LineSegment StartX=3.7 StartY=-8 StartZ=0 EndX=-3.7 EndY=-8 EndZ=0
  constraints (21):
    c: Coincident(g0,g1)
    c: Coincident(g1,g2)
    c: Coincident(g2,g3)
    c: Coincident(g3,g0)
    c: Vertical(g0)
    c: Vertical(g2)
    c: Coincident(g4,g5)
    c: Coincident(g5,g6)
    c: Coincident(g6,g7)
    c: Coincident(g7,g4)
    c: Vertical(g4)
    c: Vertical(g6)
    c: Horizontal(g5)
    c: Horizontal(g7)
    c: Symmetric(g0,g6,g-1)
    c: DistanceY(g-1,g1) = 8
    c: DistanceY(g2,g2) = 3.6
    c: DistanceX(g3,g3) = 7.4
    c: Symmetric(g2,g4,g-1)
    c: Symmetric(g1,g0,g-2)
    c: Horizontal(g3)
FEATURE [Sketcher::SketchObject] Sketch009
  ArcFitTolerance = 1e-06
  AttachmentSupport = -> [XY_Plane005]
  FullyConstrained = true
  MakeInternals = false
  MapMode = 5
  sketch-geometry (1):
    g0: Circle CenterX=0 CenterY=-6 CenterZ=0 NormalX=0 NormalY=0 NormalZ=1 AngleXU=0 Radius=2.25
  constraints (3):
    c: PointOnObject(g0,g-2)
    c: Diameter(g0) = 4.5
    c: DistanceY(g0,g-1) = 6
FEATURE [Sketcher::SketchObject] Sketch010
  ArcFitTolerance = 1e-06
  AttachmentOffset = pos=(0,0,0) rot=(1,0,0;0.392699rad)
  AttachmentSupport = -> [YZ_Plane005]
  FullyConstrained = true
  MakeInternals = false
  MapMode = 5
  Placement = pos=(0,0,0) rot=(0.639338,0.639338,0.427192;2.33414rad)
  sketch-geometry (4):
    g0: LineSegment StartX=-3 StartY=14.5 StartZ=0 EndX=-12 EndY=14.5 EndZ=0
    g1: LineSegment StartX=-12 StartY=14.5 StartZ=0 EndX=-5 EndY=44.5 EndZ=0
    g2: LineSegment StartX=-5 StartY=44.5 StartZ=0 EndX=-3 EndY=44.5 EndZ=0
    g3: LineSegment StartX=-3 StartY=44.5 StartZ=0 EndX=-3 EndY=14.5 EndZ=0
  constraints (12):
    c: Coincident(g0,g1)
    c: Coincident(g1,g2)
    c: Horizontal(g2)
    c: Coincident(g2,g3)
    c: Coincident(g3,g0)
    c: Horizontal(g0)
    c: Vertical(g3)
    c: DistanceX(g0,g-1) = 3
    c: DistanceY(g-1,g0) = 14.5
    c: DistanceY(g3,g3) = 30
    c: DistanceX(g2,g2) = 2
    c: DistanceX(g0,g0) = 9
FEATURE [Sketcher::SketchObject] Sketch011
  ArcFitTolerance = 1e-06
  AttachmentSupport = -> [XZ_Plane005]
  FullyConstrained = true
  MakeInternals = false
  MapMode = 5
  Placement = pos=(0,0,0) rot=(1,0,0;1.5708rad)
  sketch-geometry (1):
    g0: Circle CenterX=0 CenterY=52 CenterZ=0 NormalX=0 NormalY=0 NormalZ=1 AngleXU=0 Radius=2.3
  constraints (3):
    c: PointOnObject(g0,g-2)
    c: Diameter(g0) = 4.6
    c: DistanceY(g-1,g0) = 52
FEATURE [Sketcher::SketchObject] Sketch012
  ArcFitTolerance = 1e-06
  AttachmentSupport = -> [XZ_Plane005]
  FullyConstrained = true
  MakeInternals = false
  MapMode = 5
  Placement = pos=(0,0,0) rot=(1,0,0;1.5708rad)
  sketch-geometry (5):
    g0: LineSegment StartX=0 StartY=0 StartZ=0 EndX=-1.04189 EndY=5.90885 EndZ=0
    g1: LineSegment StartX=-1.04189 StartY=5.90885 StartZ=0 EndX=-0.2 EndY=5.3692 EndZ=0
    g2: LineSegment StartX=-0.2 StartY=5.3692 StartZ=0 EndX=0.2 EndY=5.3692 EndZ=0
    g3: LineSegment StartX=0.2 StartY=5.3692 StartZ=0 EndX=1.04189 EndY=5.90885 EndZ=0
    g4: LineSegment StartX=1.04189 StartY=5.90885 StartZ=0 EndX=0 EndY=0 EndZ=0
  constraints (13):
    c: Coincident(g-1,g0)
    c: Coincident(g0,g1)
    c: Coincident(g1,g2)
    c: Horizontal(g2)
    c: Coincident(g2,g3)
    c: Coincident(g3,g4)
    c: Coincident(g4,g0)
    c: Symmetric(g3,g0,g-2)
    c: Angle(g4,g0) = 0.349066
    c: DistanceX(g2,g2) = 0.4
    c: Distance(g4) = 6
    c: Distance(g3) = 1
    c: Distance(g1) = 1
FEATURE [Sketcher::SketchObject] Sketch013
  ArcFitTolerance = 1e-06
  AttachmentSupport = -> [XZ_Plane005]
  FullyConstrained = true
  MakeInternals = false
  MapMode = 5
  Placement = pos=(0,0,0) rot=(1,0,0;1.5708rad)
  sketch-geometry (2):
    g0: Circle CenterX=0 CenterY=0 CenterZ=0 NormalX=0 NormalY=0 NormalZ=1 AngleXU=0 Radius=5
    g1: Circle CenterX=0 CenterY=0 CenterZ=0 NormalX=0 NormalY=0 NormalZ=1 AngleXU=0 Radius=15
  constraints (4):
    c: Coincident(g0,g-1)
    c: Coincident(g1,g0)
    c: Diameter(g1) = 30
    c: Diameter(g0) = 10
FEATURE [Sketcher::SketchObject] Sketch014
  ArcFitTolerance = 1e-06
  AttachmentSupport = -> [XZ_Plane005]
  FullyConstrained = true
  MakeInternals = false
  MapMode = 5
  Placement = pos=(0,0,0) rot=(1,0,0;1.5708rad)
  sketch-geometry (6):
    g0: ArcOfCircle CenterX=0 CenterY=0 CenterZ=0 NormalX=0 NormalY=0 NormalZ=1 AngleXU=0 Radius=15 StartAngle=1.23918 EndAngle=1.90241
    g1: ArcOfCircle CenterX=0 CenterY=0 CenterZ=0 NormalX=0 NormalY=0 NormalZ=1 AngleXU=0 Radius=46 StartAngle=1.23918 EndAngle=1.90241
    g2: LineSegment [constr] StartX=0 StartY=0 StartZ=0 EndX=-19.5341 EndY=56.7311 EndZ=0
    g3: LineSegment [constr] StartX=0 StartY=0 StartZ=0 EndX=19.5341 EndY=56.7311 EndZ=0
    g4: LineSegment StartX=-4.88352 StartY=14.1828 StartZ=0 EndX=-14.9761 EndY=43.4939 EndZ=0
    g5: LineSegment StartX=14.9761 StartY=43.4939 StartZ=0 EndX=4.88352 EndY=14.1828 EndZ=0
  constraints (17):
    c: Coincident(g0,g-1)
    c: Coincident(g1,g0)
    c: Coincident(g2,g0)
    c: Coincident(g3,g0)
    c: Coincident(g4,g0)
    c: Coincident(g4,g1)
    c: Coincident(g5,g1)
    c: Coincident(g5,g0)
    c: Symmetric(g2,g3,g-2)
    c: Angle(g3,g2) = 0.663225
    c: PointOnObject(g0,g3)
    c: PointOnObject(g1,g3)
    c: PointOnObject(g0,g2)
    c: PointOnObject(g1,g2)
    c: Diameter(g1) = 92
    c: Diameter(g0) = 30
    c: Distance(g3) = 60
FEATURE [Sketcher::SketchObject] Sketch015
  ArcFitTolerance = 1e-06
  AttachmentSupport = -> [XZ_Plane005]
  FullyConstrained = true
  MakeInternals = false
  MapMode = 5
  Placement = pos=(0,0,0) rot=(1,0,0;1.5708rad)
  sketch-geometry (2):
    g0: Circle CenterX=0 CenterY=0 CenterZ=0 NormalX=0 NormalY=0 NormalZ=1 AngleXU=0 Radius=58
    g1: Circle CenterX=0 CenterY=0 CenterZ=0 NormalX=0 NormalY=0 NormalZ=1 AngleXU=0 Radius=5
  constraints (4):
    c: Coincident(g0,g-1)
    c: Diameter(g0) = 116
    c: Coincident(g1,g0)
    c: Diameter(g1) = 10
FEATURE [PartDesign::Pad] Pad005  label="Pad_External"
  Direction = (0,-1,2e-16)
  Length = 3
  Length2 = 10
  Placement = pos=(0,0,0) rot=(1,0,0;1.5708rad)
  Profile = -> Sketch015
  ReferenceAxis = -> Sketch015 [N_Axis]
  Refine = true
  Suppressed = false
  Type = 0
FEATURE [PartDesign::Pocket] Pocket002  label="Pocket_Gap"
  BaseFeature = -> Pad005
  Direction = (0,1,-2e-16)
  Length = 5
  Length2 = 5
  Placement = pos=(0,0,0) rot=(1,0,0;1.5708rad)
  Profile = -> Sketch014
  ReferenceAxis = -> Sketch014 [N_Axis]
  Refine = true
  Reversed = true
  Suppressed = false
  Type = 0
FEATURE [PartDesign::PolarPattern] PolarPattern  label="PolarPattern_Gaps"
  Angle = 360
  Axis = -> Sketch014 [N_Axis]
  BaseFeature = -> Pocket002
  Mode = 0
  Occurrences = 8
  Offset = 120
  Originals = -> [Pocket002]
  Placement = pos=(0,0,0) rot=(1,0,0;1.5708rad)
  Refine = true
  Suppressed = false
  TransformMode = 0
FEATURE [PartDesign::Pad] Pad006  label="Pad_Center"
  BaseFeature = -> PolarPattern
  Direction = (0,-1,2e-16)
  Length = 12
  Length2 = 10
  Placement = pos=(0,0,0) rot=(1,0,0;1.5708rad)
  Profile = -> Sketch013
  ReferenceAxis = -> Sketch013 [N_Axis]
  Refine = true
  Suppressed = false
  Type = 0
FEATURE [PartDesign::Pocket] Pocket003  label="Pocket_Shaft"
  BaseFeature = -> Pad006
  Direction = (0,1,-2e-16)
  Length = 5
  Length2 = 5
  Placement = pos=(0,0,0) rot=(1,0,0;1.5708rad)
  Profile = -> Sketch012
  ReferenceAxis = -> Sketch012 [N_Axis]
  Refine = true
  Reversed = true
  Suppressed = false
  Type = 1
FEATURE [PartDesign::PolarPattern] PolarPattern001  label="PolarPattern_DriveShaft"
  Angle = 360
  Axis = -> Sketch012 [N_Axis]
  BaseFeature = -> Pocket003
  Mode = 0
  Occurrences = 18
  Offset = 120
  Originals = -> [Pocket003]
  Placement = pos=(0,0,0) rot=(1,0,0;1.5708rad)
  Refine = true
  Suppressed = false
  TransformMode = 0
FEATURE [PartDesign::Pocket] Pocket004  label="Pocket_Screw"
  BaseFeature = -> PolarPattern001
  Direction = (0,1,-2e-16)
  Length = 5
  Length2 = 5
  Placement = pos=(0,0,0) rot=(1,0,0;1.5708rad)
  Profile = -> Sketch011
  ReferenceAxis = -> Sketch011 [N_Axis]
  Refine = true
  Reversed = true
  Suppressed = false
  Type = 1
FEATURE [PartDesign::PolarPattern] PolarPattern002  label="PolarPattern_Inertia"
  Angle = 360
  Axis = -> Sketch011 [N_Axis]
  BaseFeature = -> Pocket004
  Mode = 0
  Occurrences = 32
  Offset = 120
  Originals = -> [Pocket004]
  Placement = pos=(0,0,0) rot=(1,0,0;1.5708rad)
  Refine = true
  Suppressed = false
  TransformMode = 0
FEATURE [PartDesign::Pad] Pad007  label="Pad_Reinforcement"
  BaseFeature = -> PolarPattern002
  Direction = (0.92388,0,-0.382683)
  Length = 2
  Length2 = 10
  Midplane = true
  Placement = pos=(0,0,0) rot=(1,0,0;1.5708rad)
  Profile = -> Sketch010
  ReferenceAxis = -> Sketch010 [N_Axis]
  Refine = true
  Suppressed = false
  Type = 0
FEATURE [PartDesign::PolarPattern] PolarPattern003  label="PolarPattern_Reinforcements"
  Angle = 360
  Axis = -> Y_Axis005
  BaseFeature = -> Pad007
  Mode = 0
  Occurrences = 8
  Offset = 120
  Originals = -> [Pad007]
  Placement = pos=(0,0,0) rot=(1,0,0;1.5708rad)
  Refine = true
  Suppressed = false
  TransformMode = 0
FEATURE [PartDesign::Pocket] Pocket005  label="Pocket_Fixation"
  BaseFeature = -> PolarPattern003
  Direction = (0,0,-1)
  Length = 30
  Length2 = 5
  Midplane = true
  Placement = pos=(0,0,0) rot=(1,0,0;1.5708rad)
  Profile = -> Sketch009
  ReferenceAxis = -> Sketch009 [N_Axis]
  Refine = true
  Suppressed = false
  Type = 0
FEATURE [PartDesign::Pocket] Pocket006  label="Pocket_Bolts"
  BaseFeature = -> Pocket005
  Direction = (0,1,-2e-16)
  Length = 12
  Length2 = 5
  Placement = pos=(0,0,0) rot=(1,0,0;1.5708rad)
  Profile = -> Sketch008
  ReferenceAxis = -> Sketch008 [N_Axis]
  Refine = true
  Reversed = true
  Suppressed = false
  Type = 0
FEATURE [PartDesign::Chamfer] Chamfer001
  Angle = 45
  Base = -> Pocket006 [Edge108,Edge103,Edge102,Edge101,Edge38,Edge33,Edge32,Edge10,Edge9,Edge5,Edge6,Edge4,Edge7,Edge8,Edge15,Edge16,Edge17,Edge23,Edge24,Edge25,Edge30,Edge31,Edge123,Edge124,Edge125,Edge129,Edge128,Edge130,Edge127,Edge126,Edge110,Edge109]
  BaseFeature = -> Pocket006
  ChamferType = 0
  FlipDirection = true
  Placement = pos=(0,0,0) rot=(1,0,0;1.5708rad)
  Refine = true
  Size = 1.5
  Size2 = 1
  SupportTransform = false
  Suppressed = false
  UseAllEdges = false
FEATURE [PartDesign::CoordinateSystem] reactionWheel
  AttacherType = Attacher::AttachEngine3D
  AttachmentOffset = pos=(0,0,0) rot=(-0.57735,0.57735,-0.57735;2.0944rad)
  AttachmentSupport = -> [Chamfer001]
  MapMode = 11
  Placement = pos=(0,-12,5.3e-15) rot=(0,0,1;0rad)
FEATURE [PartDesign::Body] Body004  label="Body_ReactionWheel"
  AllowCompound = false
  Group = -> [Sketch015,Pad005,Sketch014,Pocket002,PolarPattern,Sketch013,Pad006,Sketch012,Pocket003,PolarPattern001,Sketch011,Pocket004,PolarPattern002,Sketch010,Pad007,PolarPattern003,Sketch009,Pocket005,Sketch008,Pocket006,reactionWheel,Chamfer001]
  Origin = -> Origin005
  Tip = -> Chamfer001
COMPONENT P10 — recipe-attached ("Body_Support001", modeled in this document).
Construction recipe (the document's own serialized feature program — sketch geometry with constraints, then the solid features built on it; lengths are millimeters unless a unit is written):

FEATURE [Sketcher::SketchObject] Sketch
  ArcFitTolerance = 1e-06
  AttachmentSupport = -> [XZ_Plane001]
  FullyConstrained = true
  MakeInternals = false
  MapMode = 5
  Placement = pos=(0,0,0) rot=(1,0,0;1.5708rad)
  sketch-geometry (13):
    g0: LineSegment StartX=5.6759 StartY=30.0968 StartZ=0 EndX=23.0689 EndY=6 EndZ=0
    g1: LineSegment StartX=23.0689 StartY=6 StartZ=0 EndX=34 EndY=6 EndZ=0
    g2: LineSegment StartX=34 StartY=6 StartZ=0 EndX=34 EndY=0 EndZ=0
    g3: LineSegment StartX=34 StartY=0 StartZ=0 EndX=20 EndY=0 EndZ=0
    g4: LineSegment StartX=20 StartY=0 StartZ=0 EndX=4.86567 EndY=20.9676 EndZ=0
    g5: LineSegment StartX=-4.86567 StartY=20.9676 StartZ=0 EndX=-20 EndY=0 EndZ=0
    g6: LineSegment StartX=-20 StartY=0 StartZ=0 EndX=-34 EndY=0 EndZ=0
    g7: LineSegment StartX=-34 StartY=0 StartZ=0 EndX=-34 EndY=6 EndZ=0
    g8: LineSegment StartX=-34 StartY=6 StartZ=0 EndX=-23.0689 EndY=6 EndZ=0
    g9: LineSegment StartX=-23.0689 StartY=6 StartZ=0 EndX=-5.6759 EndY=30.0968 EndZ=0
    g10: Circle CenterX=-1e-16 CenterY=26 CenterZ=0 NormalX=0 NormalY=0 NormalZ=1 AngleXU=0 Radius=2.8
    g11: ArcOfCircle CenterX=-1e-16 CenterY=26 CenterZ=0 NormalX=0 NormalY=0 NormalZ=1 AngleXU=0 Radius=7 StartAngle=0.625205 EndAngle=2.51639
    g12: ArcOfCircle CenterX=-1e-16 CenterY=26 CenterZ=0 NormalX=0 NormalY=0 NormalZ=1 AngleXU=0 Radius=7 StartAngle=3.94384 EndAngle=5.48094
  constraints (36):
    c: Coincident(g0,g1)
    c: Horizontal(g1)
    c: Coincident(g1,g2)
    c: PointOnObject(g2,g-1)
    c: Coincident(g2,g3)
    c: PointOnObject(g3,g-1)
    c: Coincident(g3,g4)
    c: Coincident(g5,g6)
    c: PointOnObject(g6,g-1)
    c: Coincident(g6,g7)
    c: Vertical(g7)
    c: Coincident(g7,g8)
    c: Horizontal(g8)
    c: Coincident(g8,g9)
    c: Symmetric(g9,g0,g-2)
    c: Parallel(g9,g5)
    c: Parallel(g0,g4)
    c: Vertical(g2)
    c: Equal(g7,g2)
    c: DistanceY(g7,g7) = 6
    c: Equal(g8,g1)
    c: DistanceX(g6,g6) = 14
    c: DistanceX(g5,g3) = 40
    c: Diameter(g10) = 5.6
    c: Coincident(g11,g10)
    c: Coincident(g11,g0)
    c: Equal(g11,g12)
    c: Coincident(g11,g12)
    c: Coincident(g4,g12)
    c: Coincident(g5,g12)
    c: DistanceY(g-1,g10) = 26
    c: Distance(g5,g9) = 6
    c: Distance(g4,g0) = 6
    c: Tangent(g9,g11) = 1.5708
    c: Diameter(g11) = 14
    c: Symmetric(g5,g3,g-2)
FEATURE [PartDesign::Pad] Pad  label="Pad_Main"
  Direction = (0,-1,2e-16)
  Length = 10
  Length2 = 10
  Placement = pos=(0,0,0) rot=(1,0,0;1.5708rad)
  Profile = -> Sketch
  ReferenceAxis = -> Sketch [N_Axis]
  Refine = true
  Suppressed = false
  Type = 0
FEATURE [Sketcher::SketchObject] Sketch001
  ArcFitTolerance = 1e-06
  AttachmentSupport = -> [Pad]
  ExternalGeometry = -> [Pad]
  FullyConstrained = true
  MakeInternals = false
  MapMode = 5
  Placement = pos=(0,-10,0) rot=(1,0,0;1.5708rad)
  sketch-geometry (2):
    g0: Circle CenterX=0 CenterY=26 CenterZ=0 NormalX=0 NormalY=0 NormalZ=1 AngleXU=0 Radius=3.8
    g1: Circle CenterX=0 CenterY=26 CenterZ=0 NormalX=0 NormalY=0 NormalZ=1 AngleXU=0 Radius=2.8
  constraints (4):
    c: Coincident(g0,g-3)
    c: Coincident(g1,g0)
    c: Diameter(g1) = 5.6
    c: Diameter(g0) = 7.6
FEATURE [PartDesign::Pad] Pad001  label="Pad_Shaft"
  BaseFeature = -> Pad
  Direction = (0,-1,2e-16)
  Length = 16.6
  Length2 = 10
  Placement = pos=(0,0,0) rot=(1,0,0;1.5708rad)
  Profile = -> Sketch001
  ReferenceAxis = -> Sketch001 [N_Axis]
  Refine = true
  Suppressed = false
  Type = 0
FEATURE [Sketcher::SketchObject] Sketch002
  ArcFitTolerance = 1e-06
  AttachmentSupport = -> [Pad001]
  ExternalGeometry = -> [Pad001]
  FullyConstrained = true
  MakeInternals = false
  MapMode = 5
  Placement = pos=(0,-10,0) rot=(1,0,0;1.5708rad)
  sketch-geometry (2):
    g0: Circle CenterX=0 CenterY=26 CenterZ=0 NormalX=0 NormalY=0 NormalZ=1 AngleXU=0 Radius=3.8
    g1: Circle CenterX=0 CenterY=26 CenterZ=0 NormalX=0 NormalY=0 NormalZ=1 AngleXU=0 Radius=6.5
  constraints (4):
    c: Coincident(g0,g-3)
    c: Equal(g0,g-3)
    c: Coincident(g1,g0)
    c: Diameter(g1) = 13
FEATURE [PartDesign::Pad] Pad002  label="Pad_Thrust"
  BaseFeature = -> Pad001
  Direction = (0,-1,2e-16)
  Length = 10
  Length2 = 10
  Placement = pos=(0,0,0) rot=(1,0,0;1.5708rad)
  Profile = -> Sketch002
  ReferenceAxis = -> Sketch002 [N_Axis]
  Refine = true
  Suppressed = false
  Type = 0
FEATURE [Sketcher::SketchObject] Sketch003
  ArcFitTolerance = 1e-06
  AttachmentSupport = -> [Pad002]
  FullyConstrained = true
  MakeInternals = false
  MapMode = 5
  Placement = pos=(0,2.9e-15,0) rot=(-1,0,0;1.5708rad)
  sketch-geometry (7):
    g0: LineSegment StartX=-4.8 StartY=-26 StartZ=0 EndX=-2.4 EndY=-30.1569 EndZ=0
    g1: LineSegment StartX=-2.4 StartY=-30.1569 StartZ=0 EndX=2.4 EndY=-30.1569 EndZ=0
    g2: LineSegment StartX=2.4 StartY=-30.1569 StartZ=0 EndX=4.8 EndY=-26 EndZ=0
    g3: LineSegment StartX=4.8 StartY=-26 StartZ=0 EndX=2.4 EndY=-21.8431 EndZ=0
    g4: LineSegment StartX=2.4 StartY=-21.8431 StartZ=0 EndX=-2.4 EndY=-21.8431 EndZ=0
    g5: LineSegment StartX=-2.4 StartY=-21.8431 StartZ=0 EndX=-4.8 EndY=-26 EndZ=0
    g6: Circle [constr] CenterX=0 CenterY=-26 CenterZ=0 NormalX=0 NormalY=0 NormalZ=1 AngleXU=0 Radius=4.8
  constraints (16):
    c: Coincident(g0,g1)
    c: Coincident(g1,g2)
    c: Coincident(g2,g3)
    c: Coincident(g3,g4)
    c: Coincident(g4,g5)
    c: Coincident(g5,g0)
    c: Equal(g0, g1-g5) x5
    c: PointOnObject(g0,g6)
    c: PointOnObject(g1,g6)
    c: PointOnObject(g2,g6)
    c: PointOnObject(g3,g6)
    c: PointOnObject(g4,g6)
    c: PointOnObject(g5,g6)
    c: Coincident(g6,g-3)
    c: Horizontal(g4)
    c: Diameter(g6) = 9.6
FEATURE [PartDesign::Pocket] Pocket
  BaseFeature = -> Pad002
  Direction = (0,-1,-2e-16)
  Length = 3
  Length2 = 5
  Placement = pos=(0,0,0) rot=(1,0,0;1.5708rad)
  Profile = -> Sketch003
  ReferenceAxis = -> Sketch003 [N_Axis]
  Refine = true
  Suppressed = false
  Type = 0
FEATURE [PartDesign::CoordinateSystem] Support
  AttacherType = Attacher::AttachEngine3D
  AttachmentOffset = pos=(0,0,0) rot=(-0.57735,0.57735,-0.57735;2.0944rad)
  AttachmentSupport = -> [Pocket]
  MapMode = 11
  Placement = pos=(0,-26.6,26) rot=(0,0,1;0rad)
FEATURE [Sketcher::SketchObject] Sketch050
  ArcFitTolerance = 1e-06
  AttachmentSupport = -> [XY_Plane001]
  FullyConstrained = true
  MakeInternals = false
  MapMode = 5
  sketch-geometry (2):
    g0: Circle CenterX=-27.5 CenterY=-5 CenterZ=0 NormalX=0 NormalY=0 NormalZ=1 AngleXU=0 Radius=2.3
    g1: Circle CenterX=27.5 CenterY=-5 CenterZ=0 NormalX=0 NormalY=0 NormalZ=1 AngleXU=0 Radius=2.3
  constraints (5):
    c: Equal(g1,g0)
    c: Diameter(g1) = 4.6
    c: DistanceX(g0,g1) = 55
    c: DistanceY(g1,g-1) = 5
    c: Symmetric(g1,g0,g-2)
FEATURE [PartDesign::Pocket] Pocket015
  BaseFeature = -> Pocket
  Direction = (0,0,-1)
  Length = 5
  Length2 = 5
  Placement = pos=(0,0,0) rot=(1,0,0;1.5708rad)
  Profile = -> Sketch050
  ReferenceAxis = -> Sketch050 [N_Axis]
  Refine = true
  Reversed = true
  Suppressed = false
  Type = 1
FEATURE [PartDesign::Chamfer] Chamfer003
  Angle = 45
  Base = -> Pocket015 [Edge47,Edge40]
  BaseFeature = -> Pocket015
  ChamferType = 0
  FlipDirection = false
  Placement = pos=(0,0,0) rot=(1,0,0;1.5708rad)
  Refine = true
  Size = 1.5
  Size2 = 1
  SupportTransform = false
  Suppressed = false
  UseAllEdges = false
FEATURE [PartDesign::CoordinateSystem] Support_Foot
  AttacherType = Attacher::AttachEngine3D
  AttachmentOffset = pos=(0,0,0) rot=(0.866025,-0.5,0;3.14159rad)
  AttachmentSupport = -> [Pocket015]
  MapMode = 11
  Placement = pos=(-27.5,-5,6) rot=(0,0,1;5.75959rad)
FEATURE [PartDesign::Fillet] Fillet010
  Base = -> Pocket015 [Edge31,Edge16,Edge13,Edge28]
  BaseFeature = -> Pocket015
  Placement = pos=(0,0,0) rot=(1,0,0;1.5708rad)
  Radius = 4.99
  Refine = true
  SupportTransform = false
  Suppressed = false
  UseAllEdges = false
FEATURE [PartDesign::Body] Body  label="Body_Support"
  AllowCompound = false
  Description = Pendulum
  Group = -> [Sketch,Pad,Sketch001,Pad001,Sketch002,Pad002,Sketch003,Pocket,Support,Sketch050,Pocket015,Chamfer003,Support_Foot,Fillet010]
  Origin = -> Origin001
  Tip = -> Fillet010
COMPONENT P11 — recipe-attached ("Body_Trepied001", modeled in this document).
Construction recipe (the document's own serialized feature program — sketch geometry with constraints, then the solid features built on it; lengths are millimeters unless a unit is written):

FEATURE [Sketcher::SketchObject] Sketch051
  ArcFitTolerance = 1e-06
  AttachmentSupport = -> [XY_Plane111]
  FullyConstrained = true
  MakeInternals = false
  MapMode = 5
  sketch-geometry (1):
    g0: Circle CenterX=0 CenterY=55 CenterZ=0 NormalX=0 NormalY=0 NormalZ=1 AngleXU=0 Radius=2.3
  constraints (3):
    c: PointOnObject(g0,g-2)
    c: DistanceY(g-1,g0) = 55
    c: Diameter(g0) = 4.6
FEATURE [Sketcher::SketchObject] Sketch052
  ArcFitTolerance = 1e-06
  AttachmentSupport = -> [XY_Plane111]
  FullyConstrained = true
  MakeInternals = false
  MapMode = 5
  sketch-geometry (1):
    g0: Circle CenterX=0 CenterY=0 CenterZ=0 NormalX=0 NormalY=0 NormalZ=1 AngleXU=0 Radius=62.5
  constraints (2):
    c: Coincident(g0,g-1)
    c: Diameter(g0) = 125
FEATURE [PartDesign::Pad] Pad032
  Direction = (0,0,1)
  Length = 3
  Length2 = 10
  Profile = -> Sketch052
  ReferenceAxis = -> Sketch052 [N_Axis]
  Refine = true
  Suppressed = false
  Type = 0
FEATURE [PartDesign::Fillet] Fillet009
  Base = -> Pad032 [Edge3,Edge2]
  BaseFeature = -> Pad032
  Radius = 1.49
  Refine = true
  SupportTransform = false
  Suppressed = false
  UseAllEdges = false
FEATURE [PartDesign::Pocket] Pocket016
  BaseFeature = -> Fillet009
  Direction = (0,0,-1)
  Length = 5
  Length2 = 5
  Profile = -> Sketch051
  ReferenceAxis = -> Sketch051 [N_Axis]
  Refine = true
  Reversed = true
  Suppressed = false
  Type = 0
FEATURE [PartDesign::PolarPattern] PolarPattern006
  Angle = 360
  Axis = -> Sketch051 [N_Axis]
  BaseFeature = -> Pocket016
  Mode = 0
  Occurrences = 6
  Offset = 120
  Originals = -> [Pocket016]
  Refine = true
  Suppressed = false
  TransformMode = 0
FEATURE [PartDesign::CoordinateSystem] Trepied
  AttacherType = Attacher::AttachEngine3D
  AttachmentOffset = pos=(0,0,0) rot=(0.707107,0.707107,0;3.14159rad)
  AttachmentSupport = -> [PolarPattern006]
  MapMode = 11
  Placement = pos=(-6.7e-15,-55,3) rot=(0,0,1;0rad)
FEATURE [Sketcher::SketchObject] Sketch053
  ArcFitTolerance = 1e-06
  AttachmentSupport = -> [PolarPattern006]
  FullyConstrained = true
  MakeInternals = false
  MapMode = 5
  Placement = pos=(0,0,3) rot=(0,0,1;0rad)
  sketch-geometry (2):
    g0: Circle CenterX=0 CenterY=0 CenterZ=0 NormalX=0 NormalY=0 NormalZ=1 AngleXU=0 Radius=37
    g1: Circle CenterX=0 CenterY=0 CenterZ=0 NormalX=0 NormalY=0 NormalZ=1 AngleXU=0 Radius=35.3
  constraints (4):
    c: Coincident(g0,g-1)
    c: Diameter(g0) = 74
    c: Coincident(g1,g0)
    c: Diameter(g1) = 70.6
FEATURE [PartDesign::Pad] Pad033
  BaseFeature = -> PolarPattern006
  Direction = (0,0,1)
  Length = 60
  Length2 = 10
  Profile = -> Sketch053
  ReferenceAxis = -> Sketch053 [N_Axis]
  Refine = true
  Reversed = true
  Suppressed = false
  Type = 0
FEATURE [PartDesign::CoordinateSystem] Trepied_Bottom
  AttacherType = Attacher::AttachEngine3D
  AttachmentOffset = pos=(0,0,0) rot=(0,0,-1;0.523599rad)
  AttachmentSupport = -> [Pad033]
  MapMode = 45
  Placement = pos=(-47.6314,27.5,3) rot=(0,0,1;0.523595rad)
FEATURE [PartDesign::CoordinateSystem] Trepied_Axial
  AttacherType = Attacher::AttachEngine3D
  AttachmentSupport = -> [Pad033]
  MapMode = 45
  Placement = pos=(1.683e-13,3.2e-15,-57) rot=(0,0,1;0rad)
FEATURE [PartDesign::Body] Body015  label="Body_Trepied"
  AllowCompound = false
  Group = -> [Sketch052,Pad032,Fillet009,Sketch051,Pocket016,PolarPattern006,Trepied,Sketch053,Pad033,Trepied_Bottom,Trepied_Axial]
  Origin = -> Origin111
  Tip = -> Pad033
COMPONENT P12 — geometry summary ("PCB"; no construction recipe available for this part):
  bounding box: 44.3 x 17.8 x 4.8 mm
  tessellated surface: 34,934 triangles
  volume: 1544 mm^3 (41% of its bounding box)
COMPONENT P13 — geometry summary ("main_Circuit-kicad"; no construction recipe available for this part):
  bounding box: 70.0 x 50.0 x 24.0 mm
  tessellated surface: 19,432 triangles
  volume: 7183 mm^3 (9% of its bounding box)
PROVENANCE & LICENSES
A FreeCAD (.FCStd) document from a public repository crawl; recipes are the document's own serialized feature recipes (and, for linked parts, companion documents' recipes).
License: gpl-3.0.
